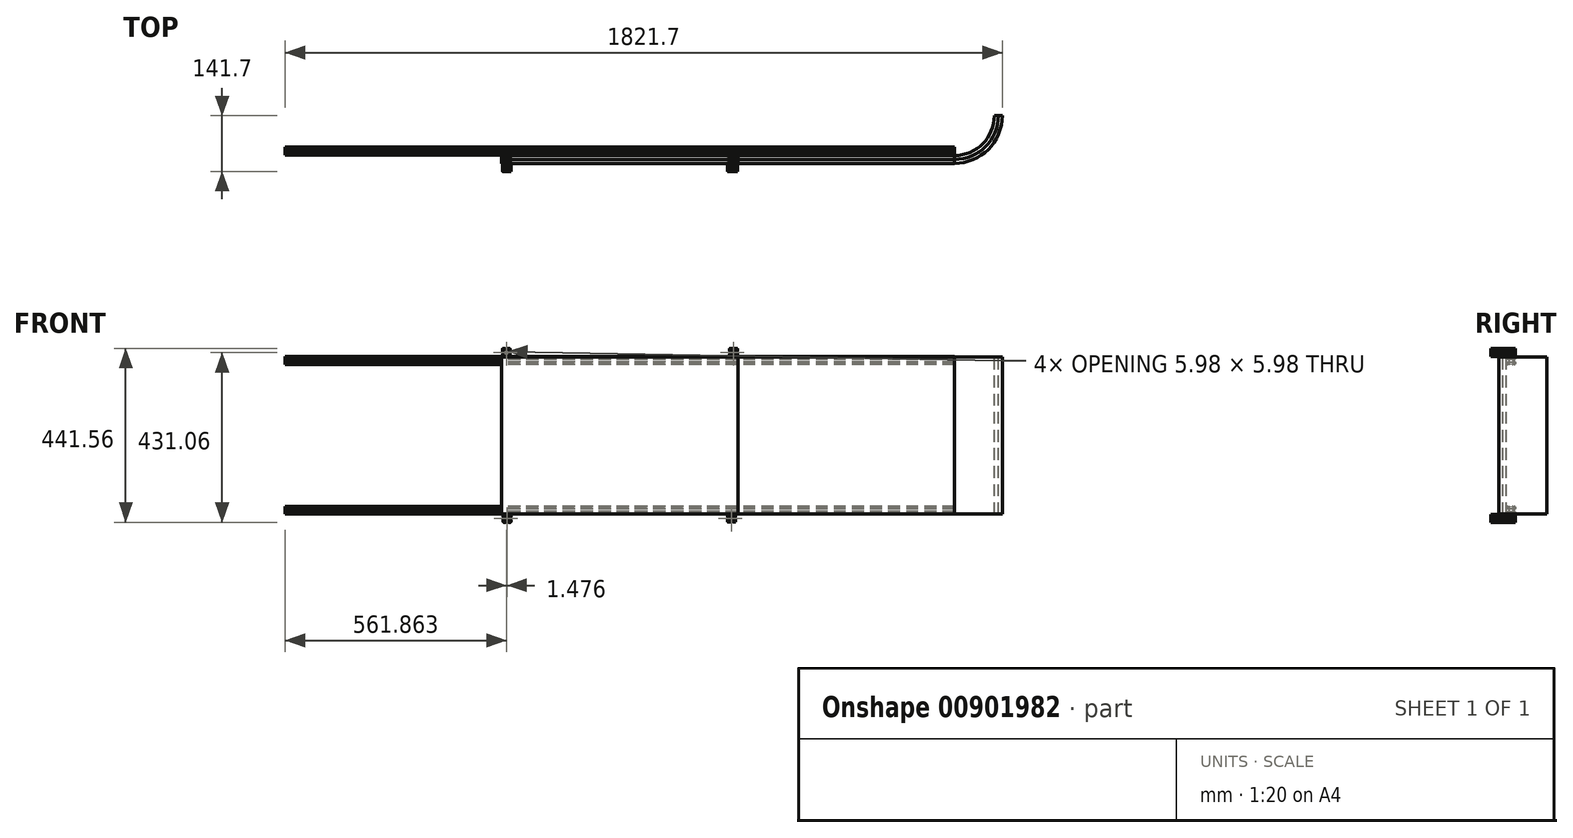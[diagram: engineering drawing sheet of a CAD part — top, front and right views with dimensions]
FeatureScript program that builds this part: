
annotation { "Feature Type Name" : "Feature", "Feature Type Description" : "" }
export const myFeature = defineFeature(function(context is Context, id is Id, definition is map)
    precondition{}
    {
        {
            var Q0;
            Q0=qCreatedBy(makeId("Front.planeOp"),FACE);
            var sketch = newSketch(context, id + "F0", { "sketchPlane" : qUnion([Q0])});
            skLineSegment(sketch, "E0.bottom", {"start": v(300, -200) * mm, "end": v(-300, -200) * mm});
            skLineSegment(sketch, "E0.top", {"start": v(300, 200) * mm, "end": v(-300, 200) * mm});
            skLineSegment(sketch, "E0.left", {"start": v(300, -200) * mm, "end": v(300, 200) * mm});
            skLineSegment(sketch, "E0.right", {"start": v(-300, -200) * mm, "end": v(-300, 200) * mm});
            skPoint(sketch, "E0.middle", {"position": v(0, 0) * mm});
            skSolve(sketch);
        }
        {
            var Q0;
            Q0=makeQuery(id+"F0.imprint","IMPRINT",FACE,{"disambiguationData":[TD([[makeQuery(id+"F0.imprint","IMPRINT",EDGE,{"derivedFrom":sQuery(id+"F0.wireOp",EDGE,"E0.bottom")}),-1.0]])]});
            extrude(context, id + "F1", {"entities" : qUnion([Q0]), "depth" : 10 * mm, "offsetDistance" : 25 * mm});
        }
        {
            var Q0;
            Q0=makeQuery(id+"F1.opExtrude","SWEPT_FACE",FACE,{"disambiguationData":[OSD([sQuery(id+"F0.wireOp",EDGE,"E0.left")])]});
            var sketch = newSketch(context, id + "F2", { "sketchPlane" : qUnion([Q0])});
            skLineSegment(sketch, "E1.bottom", {"start": v(0, -200) * mm, "end": v(-10, -200) * mm});
            skLineSegment(sketch, "E1.top", {"start": v(0, 200) * mm, "end": v(-10, 200) * mm});
            skLineSegment(sketch, "E1.left", {"start": v(0, -200) * mm, "end": v(0, 200) * mm});
            skLineSegment(sketch, "E1.right", {"start": v(-10, -200) * mm, "end": v(-10, 200) * mm});
            skSolve(sketch);
        }
        {
            var Q0;
            Q0=makeQuery(id+"F2.imprint","IMPRINT",FACE,{"disambiguationData":[TD([[makeQuery(id+"F2.imprint","IMPRINT",EDGE,{"derivedFrom":sQuery(id+"F2.wireOp",EDGE,"E1.bottom")}),1.0]])]});
            extrude(context, id + "F3", {"entities" : qUnion([Q0]), "operationType" : NewBodyOperationType.ADD, "depth" : 550 * mm, "offsetDistance" : 25 * mm, "hasSecondDirection" : true, "secondDirectionOppositeDirection" : false, "secondDirectionDepth" : 0.01 * mm});
        }
        {
            var Q0;
            Q0=makeQuery(id+"F3.opExtrude","CAP_FACE",FACE,{"disambiguationData":[OSD([sQuery(id+"F2.wireOp",EDGE,"E1.bottom"),sQuery(id+"F2.wireOp",EDGE,"E1.top"),sQuery(id+"F2.wireOp",EDGE,"E1.left"),sQuery(id+"F2.wireOp",EDGE,"E1.right")])],"isStart":false});
            var sketch = newSketch(context, id + "F4", { "sketchPlane" : qUnion([Q0])});
            skLineSegment(sketch, "E2", {"start": v(0, 0) * mm, "end": v(101.6, 0) * mm});
            skLineSegment(sketch, "E3", {"start": v(101.6, 0) * mm, "end": v(101.6, -197.22) * mm});
            skSolve(sketch);
        }
        {
            var Q0;
            {var subQ1=makeQuery(id+"F3.opExtrude","CAP_EDGE",EDGE,{"disambiguationData":[OSD([sQuery(id+"F2.wireOp",EDGE,"E1.bottom")])],"isStart":false});Q0=makeQuery(id+"F4.imprint","IMPRINT",FACE,{"disambiguationData":[TD([[makeQuery(id+"F4.imprint","IMPRINT",EDGE,{"derivedFrom":subQ1}),1.0]])]});}
            var Q1;
            Q1=sQuery(id+"F4.wireOp",EDGE,"E3");
            revolve(context, id + "F5", {"operationType" : NewBodyOperationType.ADD, "surfaceOperationType" : NewSurfaceOperationType.NEW, "entities" : qUnion([Q0]), "axis" : qUnion([Q1]), "revolveType" : RevolveType.TWO_DIRECTIONS, "angle" : 359.9 * degree, "angleBack" : 270 * degree});
        }
        {
            var Q0;
            Q0=makeQuery(id+"F1.opExtrude","SWEPT_BODY",BODY,{"disambiguationData":[OSD([sQuery(id+"F0.wireOp",EDGE,"E0.bottom"),sQuery(id+"F0.wireOp",EDGE,"E0.top"),sQuery(id+"F0.wireOp",EDGE,"E0.left"),sQuery(id+"F0.wireOp",EDGE,"E0.right")])]});
            transform(context, id + "F6", {"entities" : qUnion([Q0]), "transformType" : TransformType.TRANSLATION_3D, "dx" : 0 * mm, "dy" : -10.1 * mm, "dz" : 0 * mm, "makeCopy" : true});
        }
        {
            var Q0;
            Q0=makeQuery(id+"F3.opExtrude","SWEPT_BODY",BODY,{"disambiguationData":[OSD([sQuery(id+"F2.wireOp",EDGE,"E1.bottom"),sQuery(id+"F2.wireOp",EDGE,"E1.top"),sQuery(id+"F2.wireOp",EDGE,"E1.left"),sQuery(id+"F2.wireOp",EDGE,"E1.right")])]});
            transform(context, id + "F7", {"entities" : qUnion([Q0]), "transformType" : TransformType.TRANSLATION_3D, "dx" : 0 * mm, "dy" : -10.1 * mm, "dz" : 0 * mm, "makeCopy" : true});
        }
        {
            var Q0;
            Q0=makeQuery(id+"F7.opPattern","COPY",FACE,{"derivedFrom":makeQuery(id+"F3.opExtrude","CAP_FACE",FACE,{"disambiguationData":[OSD([sQuery(id+"F2.wireOp",EDGE,"E1.bottom"),sQuery(id+"F2.wireOp",EDGE,"E1.top"),sQuery(id+"F2.wireOp",EDGE,"E1.left"),sQuery(id+"F2.wireOp",EDGE,"E1.right")])],"isStart":false}),"instanceName":"1"});
            var Q1;
            Q1=sQuery(id+"F4.wireOp",EDGE,"E3");
            revolve(context, id + "F8", {"operationType" : NewBodyOperationType.ADD, "surfaceOperationType" : NewSurfaceOperationType.NEW, "entities" : qUnion([Q0]), "axis" : qUnion([Q1]), "revolveType" : RevolveType.TWO_DIRECTIONS, "angle" : 359.9 * degree, "angleBack" : 270 * degree});
        }
        {
            var Q0;
            Q0=makeQuery(id+"F6.opPattern","COPY",FACE,{"derivedFrom":makeQuery(id+"F1.opExtrude","SWEPT_FACE",FACE,{"disambiguationData":[OSD([sQuery(id+"F0.wireOp",EDGE,"E0.right")])]}),"instanceName":"1"});
            var sketch = newSketch(context, id + "F9", { "sketchPlane" : qUnion([Q0])});
            skArc(sketch, "E4", {"start": v(-20.11, 200.08) * mm, "mid": v(-21.17, 199.64) * mm, "end": v(-21.61, 198.58) * mm});
            skLineSegment(sketch, "E5", {"start": v(-21.61, 198.58) * mm, "end": v(-21.61, 193.83) * mm});
            skArc(sketch, "E6", {"start": v(-21.61, 193.83) * mm, "mid": v(-21.55, 193.7) * mm, "end": v(-21.41, 193.63) * mm});
            skLineSegment(sketch, "E7", {"start": v(-21.41, 193.63) * mm, "end": v(-21.31, 193.63) * mm});
            skArc(sketch, "E8", {"start": v(-21.11, 193.43) * mm, "mid": v(-21.17, 193.58) * mm, "end": v(-21.31, 193.63) * mm});
            skLineSegment(sketch, "E9", {"start": v(-21.11, 193.43) * mm, "end": v(-21.11, 193.28) * mm});
            skArc(sketch, "E10", {"start": v(-21.11, 193.28) * mm, "mid": v(-21.05, 193.14) * mm, "end": v(-20.91, 193.08) * mm});
            skLineSegment(sketch, "E11", {"start": v(-20.91, 193.08) * mm, "end": v(-20.61, 193.08) * mm});
            skArc(sketch, "E12", {"start": v(-20.61, 193.08) * mm, "mid": v(-20.26, 193.23) * mm, "end": v(-20.11, 193.58) * mm});
            skLineSegment(sketch, "E13", {"start": v(-20.11, 193.58) * mm, "end": v(-20.11, 195.58) * mm});
            skArc(sketch, "E14", {"start": v(-19.61, 196.08) * mm, "mid": v(-19.96, 195.94) * mm, "end": v(-20.11, 195.58) * mm});
            skLineSegment(sketch, "E15", {"start": v(-19.61, 196.08) * mm, "end": v(-18.88, 196.08) * mm});
            skArc(sketch, "E16", {"start": v(-18.53, 195.94) * mm, "mid": v(-18.69, 196.05) * mm, "end": v(-18.88, 196.08) * mm});
            skLineSegment(sketch, "E17", {"start": v(-18.53, 195.94) * mm, "end": v(-16.26, 193.67) * mm});
            skArc(sketch, "E18", {"start": v(-16.11, 193.32) * mm, "mid": v(-16.15, 193.5) * mm, "end": v(-16.26, 193.67) * mm});
            skLineSegment(sketch, "E19", {"start": v(-16.11, 193.32) * mm, "end": v(-16.11, 191.04) * mm});
            skArc(sketch, "E20", {"start": v(-16.11, 191.04) * mm, "mid": v(-16.1, 190.99) * mm, "end": v(-16.08, 190.94) * mm});
            skLineSegment(sketch, "E21", {"start": v(-16.08, 190.94) * mm, "end": v(-15.65, 190.18) * mm});
            skArc(sketch, "E22", {"start": v(-15.65, 189.98) * mm, "mid": v(-15.62, 190.08) * mm, "end": v(-15.65, 190.18) * mm});
            skLineSegment(sketch, "E23", {"start": v(-15.65, 189.98) * mm, "end": v(-16.08, 189.23) * mm});
            skArc(sketch, "E24", {"start": v(-16.08, 189.23) * mm, "mid": v(-16.1, 189.18) * mm, "end": v(-16.11, 189.13) * mm});
            skLineSegment(sketch, "E25", {"start": v(-16.11, 189.13) * mm, "end": v(-16.11, 186.85) * mm});
            skArc(sketch, "E26", {"start": v(-16.26, 186.5) * mm, "mid": v(-16.15, 186.66) * mm, "end": v(-16.11, 186.85) * mm});
            skLineSegment(sketch, "E27", {"start": v(-16.26, 186.5) * mm, "end": v(-18.53, 184.23) * mm});
            skArc(sketch, "E28", {"start": v(-18.88, 184.08) * mm, "mid": v(-18.69, 184.12) * mm, "end": v(-18.53, 184.23) * mm});
            skLineSegment(sketch, "E29", {"start": v(-18.88, 184.08) * mm, "end": v(-19.61, 184.08) * mm});
            skArc(sketch, "E30", {"start": v(-20.11, 184.58) * mm, "mid": v(-19.96, 184.23) * mm, "end": v(-19.61, 184.08) * mm});
            skLineSegment(sketch, "E31", {"start": v(-20.11, 184.58) * mm, "end": v(-20.11, 186.58) * mm});
            skArc(sketch, "E32", {"start": v(-20.11, 186.58) * mm, "mid": v(-20.26, 186.94) * mm, "end": v(-20.61, 187.08) * mm});
            skLineSegment(sketch, "E33", {"start": v(-20.61, 187.08) * mm, "end": v(-20.91, 187.08) * mm});
            skArc(sketch, "E34", {"start": v(-20.91, 187.08) * mm, "mid": v(-21.05, 187.03) * mm, "end": v(-21.11, 186.88) * mm});
            skLineSegment(sketch, "E35", {"start": v(-21.11, 186.88) * mm, "end": v(-21.11, 186.73) * mm});
            skArc(sketch, "E36", {"start": v(-21.31, 186.53) * mm, "mid": v(-21.17, 186.6) * mm, "end": v(-21.11, 186.73) * mm});
            skLineSegment(sketch, "E37", {"start": v(-21.31, 186.53) * mm, "end": v(-21.41, 186.53) * mm});
            skArc(sketch, "E38", {"start": v(-21.41, 186.53) * mm, "mid": v(-21.55, 186.48) * mm, "end": v(-21.61, 186.33) * mm});
            skLineSegment(sketch, "E39", {"start": v(-21.61, 186.33) * mm, "end": v(-21.61, 181.58) * mm});
            skArc(sketch, "E40", {"start": v(-21.61, 181.58) * mm, "mid": v(-21.17, 180.52) * mm, "end": v(-20.11, 180.08) * mm});
            skLineSegment(sketch, "E41", {"start": v(-20.11, 180.08) * mm, "end": v(-15.36, 180.08) * mm});
            skArc(sketch, "E42", {"start": v(-15.36, 180.08) * mm, "mid": v(-15.22, 180.14) * mm, "end": v(-15.16, 180.28) * mm});
            skLineSegment(sketch, "E43", {"start": v(-15.16, 180.28) * mm, "end": v(-15.16, 180.38) * mm});
            skArc(sketch, "E44", {"start": v(-14.96, 180.58) * mm, "mid": v(-15.1, 180.53) * mm, "end": v(-15.16, 180.38) * mm});
            skLineSegment(sketch, "E45", {"start": v(-14.96, 180.58) * mm, "end": v(-14.81, 180.58) * mm});
            skArc(sketch, "E46", {"start": v(-14.81, 180.58) * mm, "mid": v(-14.67, 180.64) * mm, "end": v(-14.61, 180.78) * mm});
            skLineSegment(sketch, "E47", {"start": v(-14.61, 180.78) * mm, "end": v(-14.61, 181.08) * mm});
            skArc(sketch, "E48", {"start": v(-14.61, 181.08) * mm, "mid": v(-14.76, 181.44) * mm, "end": v(-15.11, 181.58) * mm});
            skLineSegment(sketch, "E49", {"start": v(-15.11, 181.58) * mm, "end": v(-17.11, 181.58) * mm});
            skArc(sketch, "E50", {"start": v(-17.61, 182.08) * mm, "mid": v(-17.46, 181.73) * mm, "end": v(-17.11, 181.58) * mm});
            skLineSegment(sketch, "E51", {"start": v(-17.61, 182.08) * mm, "end": v(-17.61, 182.82) * mm});
            skArc(sketch, "E52", {"start": v(-17.46, 183.17) * mm, "mid": v(-17.57, 183) * mm, "end": v(-17.61, 182.82) * mm});
            skLineSegment(sketch, "E53", {"start": v(-17.46, 183.17) * mm, "end": v(-15.2, 185.44) * mm});
            skArc(sketch, "E54", {"start": v(-14.84, 185.58) * mm, "mid": v(-15.03, 185.55) * mm, "end": v(-15.2, 185.44) * mm});
            skLineSegment(sketch, "E55", {"start": v(-14.84, 185.58) * mm, "end": v(-12.56, 185.58) * mm});
            skArc(sketch, "E56", {"start": v(-12.56, 185.58) * mm, "mid": v(-12.51, 185.6) * mm, "end": v(-12.46, 185.61) * mm});
            skLineSegment(sketch, "E57", {"start": v(-12.46, 185.61) * mm, "end": v(-11.71, 186.05) * mm});
            skArc(sketch, "E58", {"start": v(-11.51, 186.05) * mm, "mid": v(-11.61, 186.07) * mm, "end": v(-11.71, 186.05) * mm});
            skLineSegment(sketch, "E59", {"start": v(-11.51, 186.05) * mm, "end": v(-10.76, 185.61) * mm});
            skArc(sketch, "E60", {"start": v(-10.76, 185.61) * mm, "mid": v(-10.7, 185.6) * mm, "end": v(-10.66, 185.58) * mm});
            skLineSegment(sketch, "E61", {"start": v(-10.66, 185.58) * mm, "end": v(-8.38, 185.58) * mm});
            skArc(sketch, "E62", {"start": v(-8.03, 185.44) * mm, "mid": v(-8.19, 185.55) * mm, "end": v(-8.38, 185.58) * mm});
            skLineSegment(sketch, "E63", {"start": v(-8.03, 185.44) * mm, "end": v(-5.76, 183.17) * mm});
            skArc(sketch, "E64", {"start": v(-5.61, 182.82) * mm, "mid": v(-5.65, 183) * mm, "end": v(-5.76, 183.17) * mm});
            skLineSegment(sketch, "E65", {"start": v(-5.61, 182.82) * mm, "end": v(-5.61, 182.08) * mm});
            skArc(sketch, "E66", {"start": v(-6.11, 181.58) * mm, "mid": v(-5.76, 181.73) * mm, "end": v(-5.61, 182.08) * mm});
            skLineSegment(sketch, "E67", {"start": v(-6.11, 181.58) * mm, "end": v(-8.11, 181.58) * mm});
            skArc(sketch, "E68", {"start": v(-8.11, 181.58) * mm, "mid": v(-8.46, 181.44) * mm, "end": v(-8.61, 181.08) * mm});
            skLineSegment(sketch, "E69", {"start": v(-8.61, 181.08) * mm, "end": v(-8.61, 180.78) * mm});
            skArc(sketch, "E70", {"start": v(-8.61, 180.78) * mm, "mid": v(-8.55, 180.64) * mm, "end": v(-8.41, 180.58) * mm});
            skLineSegment(sketch, "E71", {"start": v(-8.41, 180.58) * mm, "end": v(-8.26, 180.58) * mm});
            skArc(sketch, "E72", {"start": v(-8.06, 180.38) * mm, "mid": v(-8.12, 180.53) * mm, "end": v(-8.26, 180.58) * mm});
            skLineSegment(sketch, "E73", {"start": v(-8.06, 180.38) * mm, "end": v(-8.06, 180.28) * mm});
            skArc(sketch, "E74", {"start": v(-8.06, 180.28) * mm, "mid": v(-8, 180.14) * mm, "end": v(-7.86, 180.08) * mm});
            skLineSegment(sketch, "E75", {"start": v(-7.86, 180.08) * mm, "end": v(-3.11, 180.08) * mm});
            skArc(sketch, "E76", {"start": v(-3.11, 180.08) * mm, "mid": v(-2.05, 180.52) * mm, "end": v(-1.61, 181.58) * mm});
            skLineSegment(sketch, "E77", {"start": v(-1.61, 181.58) * mm, "end": v(-1.61, 186.33) * mm});
            skArc(sketch, "E78", {"start": v(-1.61, 186.33) * mm, "mid": v(-1.67, 186.48) * mm, "end": v(-1.81, 186.53) * mm});
            skLineSegment(sketch, "E79", {"start": v(-1.81, 186.53) * mm, "end": v(-1.91, 186.53) * mm});
            skArc(sketch, "E80", {"start": v(-2.11, 186.73) * mm, "mid": v(-2.05, 186.6) * mm, "end": v(-1.91, 186.53) * mm});
            skLineSegment(sketch, "E81", {"start": v(-2.11, 186.73) * mm, "end": v(-2.11, 186.88) * mm});
            skArc(sketch, "E82", {"start": v(-2.11, 186.88) * mm, "mid": v(-2.17, 187.03) * mm, "end": v(-2.31, 187.08) * mm});
            skLineSegment(sketch, "E83", {"start": v(-2.31, 187.08) * mm, "end": v(-2.61, 187.08) * mm});
            skArc(sketch, "E84", {"start": v(-2.61, 187.08) * mm, "mid": v(-2.96, 186.94) * mm, "end": v(-3.11, 186.58) * mm});
            skLineSegment(sketch, "E85", {"start": v(-3.11, 186.58) * mm, "end": v(-3.11, 184.58) * mm});
            skArc(sketch, "E86", {"start": v(-3.61, 184.08) * mm, "mid": v(-3.26, 184.23) * mm, "end": v(-3.11, 184.58) * mm});
            skLineSegment(sketch, "E87", {"start": v(-3.61, 184.08) * mm, "end": v(-4.34, 184.08) * mm});
            skArc(sketch, "E88", {"start": v(-4.7, 184.23) * mm, "mid": v(-4.53, 184.12) * mm, "end": v(-4.34, 184.08) * mm});
            skLineSegment(sketch, "E89", {"start": v(-4.7, 184.23) * mm, "end": v(-6.96, 186.5) * mm});
            skArc(sketch, "E90", {"start": v(-7.11, 186.85) * mm, "mid": v(-7.07, 186.66) * mm, "end": v(-6.96, 186.5) * mm});
            skLineSegment(sketch, "E91", {"start": v(-7.11, 186.85) * mm, "end": v(-7.11, 189.13) * mm});
            skArc(sketch, "E92", {"start": v(-7.11, 189.13) * mm, "mid": v(-7.12, 189.18) * mm, "end": v(-7.14, 189.23) * mm});
            skLineSegment(sketch, "E93", {"start": v(-7.14, 189.23) * mm, "end": v(-7.57, 189.98) * mm});
            skArc(sketch, "E94", {"start": v(-7.57, 190.18) * mm, "mid": v(-7.6, 190.08) * mm, "end": v(-7.57, 189.98) * mm});
            skLineSegment(sketch, "E95", {"start": v(-7.57, 190.18) * mm, "end": v(-7.14, 190.94) * mm});
            skArc(sketch, "E96", {"start": v(-7.14, 190.94) * mm, "mid": v(-7.12, 190.99) * mm, "end": v(-7.11, 191.04) * mm});
            skLineSegment(sketch, "E97", {"start": v(-7.11, 191.04) * mm, "end": v(-7.11, 193.32) * mm});
            skArc(sketch, "E98", {"start": v(-6.96, 193.67) * mm, "mid": v(-7.07, 193.5) * mm, "end": v(-7.11, 193.32) * mm});
            skLineSegment(sketch, "E99", {"start": v(-6.96, 193.67) * mm, "end": v(-4.7, 195.94) * mm});
            skArc(sketch, "E100", {"start": v(-4.34, 196.08) * mm, "mid": v(-4.53, 196.05) * mm, "end": v(-4.7, 195.94) * mm});
            skLineSegment(sketch, "E101", {"start": v(-4.34, 196.08) * mm, "end": v(-3.61, 196.08) * mm});
            skArc(sketch, "E102", {"start": v(-3.11, 195.58) * mm, "mid": v(-3.26, 195.94) * mm, "end": v(-3.61, 196.08) * mm});
            skLineSegment(sketch, "E103", {"start": v(-3.11, 195.58) * mm, "end": v(-3.11, 193.58) * mm});
            skArc(sketch, "E104", {"start": v(-3.11, 193.58) * mm, "mid": v(-2.96, 193.23) * mm, "end": v(-2.61, 193.08) * mm});
            skLineSegment(sketch, "E105", {"start": v(-2.61, 193.08) * mm, "end": v(-2.31, 193.08) * mm});
            skArc(sketch, "E106", {"start": v(-2.31, 193.08) * mm, "mid": v(-2.17, 193.14) * mm, "end": v(-2.11, 193.28) * mm});
            skLineSegment(sketch, "E107", {"start": v(-2.11, 193.28) * mm, "end": v(-2.11, 193.43) * mm});
            skArc(sketch, "E108", {"start": v(-1.91, 193.63) * mm, "mid": v(-2.05, 193.58) * mm, "end": v(-2.11, 193.43) * mm});
            skLineSegment(sketch, "E109", {"start": v(-1.91, 193.63) * mm, "end": v(-1.81, 193.63) * mm});
            skArc(sketch, "E110", {"start": v(-1.81, 193.63) * mm, "mid": v(-1.67, 193.7) * mm, "end": v(-1.61, 193.83) * mm});
            skLineSegment(sketch, "E111", {"start": v(-1.61, 193.83) * mm, "end": v(-1.61, 198.58) * mm});
            skArc(sketch, "E112", {"start": v(-1.61, 198.58) * mm, "mid": v(-2.05, 199.64) * mm, "end": v(-3.11, 200.08) * mm});
            skLineSegment(sketch, "E113", {"start": v(-3.11, 200.08) * mm, "end": v(-7.86, 200.08) * mm});
            skArc(sketch, "E114", {"start": v(-7.86, 200.08) * mm, "mid": v(-8, 200.03) * mm, "end": v(-8.06, 199.88) * mm});
            skLineSegment(sketch, "E115", {"start": v(-8.06, 199.88) * mm, "end": v(-8.06, 199.78) * mm});
            skArc(sketch, "E116", {"start": v(-8.26, 199.58) * mm, "mid": v(-8.12, 199.64) * mm, "end": v(-8.06, 199.78) * mm});
            skLineSegment(sketch, "E117", {"start": v(-8.26, 199.58) * mm, "end": v(-8.41, 199.58) * mm});
            skArc(sketch, "E118", {"start": v(-8.41, 199.58) * mm, "mid": v(-8.55, 199.53) * mm, "end": v(-8.61, 199.38) * mm});
            skLineSegment(sketch, "E119", {"start": v(-8.61, 199.38) * mm, "end": v(-8.61, 199.08) * mm});
            skArc(sketch, "E120", {"start": v(-8.61, 199.08) * mm, "mid": v(-8.46, 198.73) * mm, "end": v(-8.11, 198.58) * mm});
            skLineSegment(sketch, "E121", {"start": v(-8.11, 198.58) * mm, "end": v(-6.11, 198.58) * mm});
            skArc(sketch, "E122", {"start": v(-5.61, 198.08) * mm, "mid": v(-5.76, 198.44) * mm, "end": v(-6.11, 198.58) * mm});
            skLineSegment(sketch, "E123", {"start": v(-5.61, 198.08) * mm, "end": v(-5.61, 197.35) * mm});
            skArc(sketch, "E124", {"start": v(-5.76, 197) * mm, "mid": v(-5.65, 197.16) * mm, "end": v(-5.61, 197.35) * mm});
            skLineSegment(sketch, "E125", {"start": v(-5.76, 197) * mm, "end": v(-8.03, 194.73) * mm});
            skArc(sketch, "E126", {"start": v(-8.38, 194.58) * mm, "mid": v(-8.19, 194.62) * mm, "end": v(-8.03, 194.73) * mm});
            skLineSegment(sketch, "E127", {"start": v(-8.38, 194.58) * mm, "end": v(-10.66, 194.58) * mm});
            skArc(sketch, "E128", {"start": v(-10.66, 194.58) * mm, "mid": v(-10.7, 194.58) * mm, "end": v(-10.76, 194.56) * mm});
            skLineSegment(sketch, "E129", {"start": v(-10.76, 194.56) * mm, "end": v(-11.51, 194.12) * mm});
            skArc(sketch, "E130", {"start": v(-11.71, 194.12) * mm, "mid": v(-11.61, 194.1) * mm, "end": v(-11.51, 194.12) * mm});
            skLineSegment(sketch, "E131", {"start": v(-11.71, 194.12) * mm, "end": v(-12.46, 194.56) * mm});
            skArc(sketch, "E132", {"start": v(-12.46, 194.56) * mm, "mid": v(-12.51, 194.58) * mm, "end": v(-12.56, 194.58) * mm});
            skLineSegment(sketch, "E133", {"start": v(-12.56, 194.58) * mm, "end": v(-14.84, 194.58) * mm});
            skArc(sketch, "E134", {"start": v(-15.2, 194.73) * mm, "mid": v(-15.03, 194.62) * mm, "end": v(-14.84, 194.58) * mm});
            skLineSegment(sketch, "E135", {"start": v(-15.2, 194.73) * mm, "end": v(-17.46, 197) * mm});
            skArc(sketch, "E136", {"start": v(-17.61, 197.35) * mm, "mid": v(-17.57, 197.16) * mm, "end": v(-17.46, 197) * mm});
            skLineSegment(sketch, "E137", {"start": v(-17.61, 197.35) * mm, "end": v(-17.61, 198.08) * mm});
            skArc(sketch, "E138", {"start": v(-17.11, 198.58) * mm, "mid": v(-17.46, 198.44) * mm, "end": v(-17.61, 198.08) * mm});
            skLineSegment(sketch, "E139", {"start": v(-17.11, 198.58) * mm, "end": v(-15.11, 198.58) * mm});
            skArc(sketch, "E140", {"start": v(-15.11, 198.58) * mm, "mid": v(-14.76, 198.73) * mm, "end": v(-14.61, 199.08) * mm});
            skLineSegment(sketch, "E141", {"start": v(-14.61, 199.08) * mm, "end": v(-14.61, 199.38) * mm});
            skArc(sketch, "E142", {"start": v(-14.61, 199.38) * mm, "mid": v(-14.67, 199.53) * mm, "end": v(-14.81, 199.58) * mm});
            skLineSegment(sketch, "E143", {"start": v(-14.81, 199.58) * mm, "end": v(-14.96, 199.58) * mm});
            skArc(sketch, "E144", {"start": v(-15.16, 199.78) * mm, "mid": v(-15.1, 199.64) * mm, "end": v(-14.96, 199.58) * mm});
            skLineSegment(sketch, "E145", {"start": v(-15.16, 199.78) * mm, "end": v(-15.16, 199.88) * mm});
            skArc(sketch, "E146", {"start": v(-15.16, 199.88) * mm, "mid": v(-15.22, 200.03) * mm, "end": v(-15.36, 200.08) * mm});
            skLineSegment(sketch, "E147", {"start": v(-15.36, 200.08) * mm, "end": v(-20.11, 200.08) * mm});
            skArc(sketch, "E148", {"start": v(-13.52, 193.07) * mm, "mid": v(-14.12, 192.6) * mm, "end": v(-14.6, 192) * mm});
            skLineSegment(sketch, "E149", {"start": v(-12.87, 192.53) * mm, "end": v(-13.52, 193.07) * mm});
            skArc(sketch, "E150", {"start": v(-10.35, 192.53) * mm, "mid": v(-11.61, 192.83) * mm, "end": v(-12.87, 192.53) * mm});
            skLineSegment(sketch, "E151", {"start": v(-9.7, 193.07) * mm, "end": v(-10.35, 192.53) * mm});
            skArc(sketch, "E152", {"start": v(-8.62, 192) * mm, "mid": v(-9.1, 192.6) * mm, "end": v(-9.7, 193.07) * mm});
            skLineSegment(sketch, "E153", {"start": v(-9.17, 191.34) * mm, "end": v(-8.62, 192) * mm});
            skArc(sketch, "E154", {"start": v(-9.17, 188.83) * mm, "mid": v(-8.86, 190.08) * mm, "end": v(-9.17, 191.34) * mm});
            skLineSegment(sketch, "E155", {"start": v(-8.62, 188.17) * mm, "end": v(-9.17, 188.83) * mm});
            skArc(sketch, "E156", {"start": v(-9.7, 187.1) * mm, "mid": v(-9.1, 187.58) * mm, "end": v(-8.62, 188.17) * mm});
            skLineSegment(sketch, "E157", {"start": v(-10.35, 187.64) * mm, "end": v(-9.7, 187.1) * mm});
            skArc(sketch, "E158", {"start": v(-12.87, 187.64) * mm, "mid": v(-11.61, 187.33) * mm, "end": v(-10.35, 187.64) * mm});
            skLineSegment(sketch, "E159", {"start": v(-13.52, 187.1) * mm, "end": v(-12.87, 187.64) * mm});
            skArc(sketch, "E160", {"start": v(-14.6, 188.17) * mm, "mid": v(-14.12, 187.58) * mm, "end": v(-13.52, 187.1) * mm});
            skLineSegment(sketch, "E161", {"start": v(-14.06, 188.83) * mm, "end": v(-14.6, 188.17) * mm});
            skArc(sketch, "E162", {"start": v(-14.06, 191.34) * mm, "mid": v(-14.36, 190.08) * mm, "end": v(-14.06, 188.83) * mm});
            skLineSegment(sketch, "E163", {"start": v(-14.6, 192) * mm, "end": v(-14.06, 191.34) * mm});
            skArc(sketch, "E164", {"start": v(-20.11, -180) * mm, "mid": v(-21.17, -180.44) * mm, "end": v(-21.61, -181.5) * mm});
            skLineSegment(sketch, "E165", {"start": v(-21.61, -181.5) * mm, "end": v(-21.61, -186.25) * mm});
            skArc(sketch, "E166", {"start": v(-21.61, -186.25) * mm, "mid": v(-21.55, -186.4) * mm, "end": v(-21.41, -186.45) * mm});
            skLineSegment(sketch, "E167", {"start": v(-21.41, -186.45) * mm, "end": v(-21.31, -186.45) * mm});
            skArc(sketch, "E168", {"start": v(-21.11, -186.65) * mm, "mid": v(-21.17, -186.5) * mm, "end": v(-21.31, -186.45) * mm});
            skLineSegment(sketch, "E169", {"start": v(-21.11, -186.65) * mm, "end": v(-21.11, -186.8) * mm});
            skArc(sketch, "E170", {"start": v(-21.11, -186.8) * mm, "mid": v(-21.05, -186.94) * mm, "end": v(-20.91, -187) * mm});
            skLineSegment(sketch, "E171", {"start": v(-20.91, -187) * mm, "end": v(-20.61, -187) * mm});
            skArc(sketch, "E172", {"start": v(-20.61, -187) * mm, "mid": v(-20.26, -186.85) * mm, "end": v(-20.11, -186.5) * mm});
            skLineSegment(sketch, "E173", {"start": v(-20.11, -186.5) * mm, "end": v(-20.11, -184.5) * mm});
            skArc(sketch, "E174", {"start": v(-19.61, -184) * mm, "mid": v(-19.96, -184.15) * mm, "end": v(-20.11, -184.5) * mm});
            skLineSegment(sketch, "E175", {"start": v(-19.61, -184) * mm, "end": v(-18.88, -184) * mm});
            skArc(sketch, "E176", {"start": v(-18.53, -184.15) * mm, "mid": v(-18.69, -184.04) * mm, "end": v(-18.88, -184) * mm});
            skLineSegment(sketch, "E177", {"start": v(-18.53, -184.15) * mm, "end": v(-16.26, -186.41) * mm});
            skArc(sketch, "E178", {"start": v(-16.11, -186.77) * mm, "mid": v(-16.15, -186.58) * mm, "end": v(-16.26, -186.41) * mm});
            skLineSegment(sketch, "E179", {"start": v(-16.11, -186.77) * mm, "end": v(-16.11, -189.05) * mm});
            skArc(sketch, "E180", {"start": v(-16.11, -189.05) * mm, "mid": v(-16.1, -189.1) * mm, "end": v(-16.08, -189.15) * mm});
            skLineSegment(sketch, "E181", {"start": v(-16.08, -189.15) * mm, "end": v(-15.65, -189.9) * mm});
            skArc(sketch, "E182", {"start": v(-15.65, -190.1) * mm, "mid": v(-15.62, -190) * mm, "end": v(-15.65, -189.9) * mm});
            skLineSegment(sketch, "E183", {"start": v(-15.65, -190.1) * mm, "end": v(-16.08, -190.85) * mm});
            skArc(sketch, "E184", {"start": v(-16.08, -190.85) * mm, "mid": v(-16.1, -190.9) * mm, "end": v(-16.11, -190.95) * mm});
            skLineSegment(sketch, "E185", {"start": v(-16.11, -190.95) * mm, "end": v(-16.11, -193.23) * mm});
            skArc(sketch, "E186", {"start": v(-16.26, -193.59) * mm, "mid": v(-16.15, -193.42) * mm, "end": v(-16.11, -193.23) * mm});
            skLineSegment(sketch, "E187", {"start": v(-16.26, -193.59) * mm, "end": v(-18.53, -195.85) * mm});
            skArc(sketch, "E188", {"start": v(-18.88, -196) * mm, "mid": v(-18.69, -195.96) * mm, "end": v(-18.53, -195.85) * mm});
            skLineSegment(sketch, "E189", {"start": v(-18.88, -196) * mm, "end": v(-19.61, -196) * mm});
            skArc(sketch, "E190", {"start": v(-20.11, -195.5) * mm, "mid": v(-19.96, -195.85) * mm, "end": v(-19.61, -196) * mm});
            skLineSegment(sketch, "E191", {"start": v(-20.11, -195.5) * mm, "end": v(-20.11, -193.5) * mm});
            skArc(sketch, "E192", {"start": v(-20.11, -193.5) * mm, "mid": v(-20.26, -193.15) * mm, "end": v(-20.61, -193) * mm});
            skLineSegment(sketch, "E193", {"start": v(-20.61, -193) * mm, "end": v(-20.91, -193) * mm});
            skArc(sketch, "E194", {"start": v(-20.91, -193) * mm, "mid": v(-21.05, -193.06) * mm, "end": v(-21.11, -193.2) * mm});
            skLineSegment(sketch, "E195", {"start": v(-21.11, -193.2) * mm, "end": v(-21.11, -193.35) * mm});
            skArc(sketch, "E196", {"start": v(-21.31, -193.55) * mm, "mid": v(-21.17, -193.5) * mm, "end": v(-21.11, -193.35) * mm});
            skLineSegment(sketch, "E197", {"start": v(-21.31, -193.55) * mm, "end": v(-21.41, -193.55) * mm});
            skArc(sketch, "E198", {"start": v(-21.41, -193.55) * mm, "mid": v(-21.55, -193.6) * mm, "end": v(-21.61, -193.75) * mm});
            skLineSegment(sketch, "E199", {"start": v(-21.61, -193.75) * mm, "end": v(-21.61, -198.5) * mm});
            skArc(sketch, "E200", {"start": v(-21.61, -198.5) * mm, "mid": v(-21.17, -199.56) * mm, "end": v(-20.11, -200) * mm});
            skLineSegment(sketch, "E201", {"start": v(-20.11, -200) * mm, "end": v(-15.36, -200) * mm});
            skArc(sketch, "E202", {"start": v(-15.36, -200) * mm, "mid": v(-15.22, -199.94) * mm, "end": v(-15.16, -199.8) * mm});
            skLineSegment(sketch, "E203", {"start": v(-15.16, -199.8) * mm, "end": v(-15.16, -199.7) * mm});
            skArc(sketch, "E204", {"start": v(-14.96, -199.5) * mm, "mid": v(-15.1, -199.56) * mm, "end": v(-15.16, -199.7) * mm});
            skLineSegment(sketch, "E205", {"start": v(-14.96, -199.5) * mm, "end": v(-14.81, -199.5) * mm});
            skArc(sketch, "E206", {"start": v(-14.81, -199.5) * mm, "mid": v(-14.67, -199.44) * mm, "end": v(-14.61, -199.3) * mm});
            skLineSegment(sketch, "E207", {"start": v(-14.61, -199.3) * mm, "end": v(-14.61, -199) * mm});
            skArc(sketch, "E208", {"start": v(-14.61, -199) * mm, "mid": v(-14.76, -198.65) * mm, "end": v(-15.11, -198.5) * mm});
            skLineSegment(sketch, "E209", {"start": v(-15.11, -198.5) * mm, "end": v(-17.11, -198.5) * mm});
            skArc(sketch, "E210", {"start": v(-17.61, -198) * mm, "mid": v(-17.46, -198.35) * mm, "end": v(-17.11, -198.5) * mm});
            skLineSegment(sketch, "E211", {"start": v(-17.61, -198) * mm, "end": v(-17.61, -197.27) * mm});
            skArc(sketch, "E212", {"start": v(-17.46, -196.91) * mm, "mid": v(-17.57, -197.08) * mm, "end": v(-17.61, -197.27) * mm});
            skLineSegment(sketch, "E213", {"start": v(-17.46, -196.91) * mm, "end": v(-15.2, -194.65) * mm});
            skArc(sketch, "E214", {"start": v(-14.84, -194.5) * mm, "mid": v(-15.03, -194.54) * mm, "end": v(-15.2, -194.65) * mm});
            skLineSegment(sketch, "E215", {"start": v(-14.84, -194.5) * mm, "end": v(-12.56, -194.5) * mm});
            skArc(sketch, "E216", {"start": v(-12.56, -194.5) * mm, "mid": v(-12.51, -194.5) * mm, "end": v(-12.46, -194.47) * mm});
            skLineSegment(sketch, "E217", {"start": v(-12.46, -194.47) * mm, "end": v(-11.71, -194.04) * mm});
            skArc(sketch, "E218", {"start": v(-11.51, -194.04) * mm, "mid": v(-11.61, -194.01) * mm, "end": v(-11.71, -194.04) * mm});
            skLineSegment(sketch, "E219", {"start": v(-11.51, -194.04) * mm, "end": v(-10.76, -194.47) * mm});
            skArc(sketch, "E220", {"start": v(-10.76, -194.47) * mm, "mid": v(-10.7, -194.5) * mm, "end": v(-10.66, -194.5) * mm});
            skLineSegment(sketch, "E221", {"start": v(-10.66, -194.5) * mm, "end": v(-8.38, -194.5) * mm});
            skArc(sketch, "E222", {"start": v(-8.03, -194.65) * mm, "mid": v(-8.19, -194.54) * mm, "end": v(-8.38, -194.5) * mm});
            skLineSegment(sketch, "E223", {"start": v(-8.03, -194.65) * mm, "end": v(-5.76, -196.91) * mm});
            skArc(sketch, "E224", {"start": v(-5.61, -197.27) * mm, "mid": v(-5.65, -197.08) * mm, "end": v(-5.76, -196.91) * mm});
            skLineSegment(sketch, "E225", {"start": v(-5.61, -197.27) * mm, "end": v(-5.61, -198) * mm});
            skArc(sketch, "E226", {"start": v(-6.11, -198.5) * mm, "mid": v(-5.76, -198.35) * mm, "end": v(-5.61, -198) * mm});
            skLineSegment(sketch, "E227", {"start": v(-6.11, -198.5) * mm, "end": v(-8.11, -198.5) * mm});
            skArc(sketch, "E228", {"start": v(-8.11, -198.5) * mm, "mid": v(-8.46, -198.65) * mm, "end": v(-8.61, -199) * mm});
            skLineSegment(sketch, "E229", {"start": v(-8.61, -199) * mm, "end": v(-8.61, -199.3) * mm});
            skArc(sketch, "E230", {"start": v(-8.61, -199.3) * mm, "mid": v(-8.55, -199.44) * mm, "end": v(-8.41, -199.5) * mm});
            skLineSegment(sketch, "E231", {"start": v(-8.41, -199.5) * mm, "end": v(-8.26, -199.5) * mm});
            skArc(sketch, "E232", {"start": v(-8.06, -199.7) * mm, "mid": v(-8.12, -199.56) * mm, "end": v(-8.26, -199.5) * mm});
            skLineSegment(sketch, "E233", {"start": v(-8.06, -199.7) * mm, "end": v(-8.06, -199.8) * mm});
            skArc(sketch, "E234", {"start": v(-8.06, -199.8) * mm, "mid": v(-8, -199.94) * mm, "end": v(-7.86, -200) * mm});
            skLineSegment(sketch, "E235", {"start": v(-7.86, -200) * mm, "end": v(-3.11, -200) * mm});
            skArc(sketch, "E236", {"start": v(-3.11, -200) * mm, "mid": v(-2.05, -199.56) * mm, "end": v(-1.61, -198.5) * mm});
            skLineSegment(sketch, "E237", {"start": v(-1.61, -198.5) * mm, "end": v(-1.61, -193.75) * mm});
            skArc(sketch, "E238", {"start": v(-1.61, -193.75) * mm, "mid": v(-1.67, -193.6) * mm, "end": v(-1.81, -193.55) * mm});
            skLineSegment(sketch, "E239", {"start": v(-1.81, -193.55) * mm, "end": v(-1.91, -193.55) * mm});
            skArc(sketch, "E240", {"start": v(-2.11, -193.35) * mm, "mid": v(-2.05, -193.5) * mm, "end": v(-1.91, -193.55) * mm});
            skLineSegment(sketch, "E241", {"start": v(-2.11, -193.35) * mm, "end": v(-2.11, -193.2) * mm});
            skArc(sketch, "E242", {"start": v(-2.11, -193.2) * mm, "mid": v(-2.17, -193.06) * mm, "end": v(-2.31, -193) * mm});
            skLineSegment(sketch, "E243", {"start": v(-2.31, -193) * mm, "end": v(-2.61, -193) * mm});
            skArc(sketch, "E244", {"start": v(-2.61, -193) * mm, "mid": v(-2.96, -193.15) * mm, "end": v(-3.11, -193.5) * mm});
            skLineSegment(sketch, "E245", {"start": v(-3.11, -193.5) * mm, "end": v(-3.11, -195.5) * mm});
            skArc(sketch, "E246", {"start": v(-3.61, -196) * mm, "mid": v(-3.26, -195.85) * mm, "end": v(-3.11, -195.5) * mm});
            skLineSegment(sketch, "E247", {"start": v(-3.61, -196) * mm, "end": v(-4.34, -196) * mm});
            skArc(sketch, "E248", {"start": v(-4.7, -195.85) * mm, "mid": v(-4.53, -195.96) * mm, "end": v(-4.34, -196) * mm});
            skLineSegment(sketch, "E249", {"start": v(-4.7, -195.85) * mm, "end": v(-6.96, -193.59) * mm});
            skArc(sketch, "E250", {"start": v(-7.11, -193.23) * mm, "mid": v(-7.07, -193.42) * mm, "end": v(-6.96, -193.59) * mm});
            skLineSegment(sketch, "E251", {"start": v(-7.11, -193.23) * mm, "end": v(-7.11, -190.95) * mm});
            skArc(sketch, "E252", {"start": v(-7.11, -190.95) * mm, "mid": v(-7.12, -190.9) * mm, "end": v(-7.14, -190.85) * mm});
            skLineSegment(sketch, "E253", {"start": v(-7.14, -190.85) * mm, "end": v(-7.57, -190.1) * mm});
            skArc(sketch, "E254", {"start": v(-7.57, -189.9) * mm, "mid": v(-7.6, -190) * mm, "end": v(-7.57, -190.1) * mm});
            skLineSegment(sketch, "E255", {"start": v(-7.57, -189.9) * mm, "end": v(-7.14, -189.15) * mm});
            skArc(sketch, "E256", {"start": v(-7.14, -189.15) * mm, "mid": v(-7.12, -189.1) * mm, "end": v(-7.11, -189.05) * mm});
            skLineSegment(sketch, "E257", {"start": v(-7.11, -189.05) * mm, "end": v(-7.11, -186.77) * mm});
            skArc(sketch, "E258", {"start": v(-6.96, -186.41) * mm, "mid": v(-7.07, -186.58) * mm, "end": v(-7.11, -186.77) * mm});
            skLineSegment(sketch, "E259", {"start": v(-6.96, -186.41) * mm, "end": v(-4.7, -184.15) * mm});
            skArc(sketch, "E260", {"start": v(-4.34, -184) * mm, "mid": v(-4.53, -184.04) * mm, "end": v(-4.7, -184.15) * mm});
            skLineSegment(sketch, "E261", {"start": v(-4.34, -184) * mm, "end": v(-3.61, -184) * mm});
            skArc(sketch, "E262", {"start": v(-3.11, -184.5) * mm, "mid": v(-3.26, -184.15) * mm, "end": v(-3.61, -184) * mm});
            skLineSegment(sketch, "E263", {"start": v(-3.11, -184.5) * mm, "end": v(-3.11, -186.5) * mm});
            skArc(sketch, "E264", {"start": v(-3.11, -186.5) * mm, "mid": v(-2.96, -186.85) * mm, "end": v(-2.61, -187) * mm});
            skLineSegment(sketch, "E265", {"start": v(-2.61, -187) * mm, "end": v(-2.31, -187) * mm});
            skArc(sketch, "E266", {"start": v(-2.31, -187) * mm, "mid": v(-2.17, -186.94) * mm, "end": v(-2.11, -186.8) * mm});
            skLineSegment(sketch, "E267", {"start": v(-2.11, -186.8) * mm, "end": v(-2.11, -186.65) * mm});
            skArc(sketch, "E268", {"start": v(-1.91, -186.45) * mm, "mid": v(-2.05, -186.5) * mm, "end": v(-2.11, -186.65) * mm});
            skLineSegment(sketch, "E269", {"start": v(-1.91, -186.45) * mm, "end": v(-1.81, -186.45) * mm});
            skArc(sketch, "E270", {"start": v(-1.81, -186.45) * mm, "mid": v(-1.67, -186.4) * mm, "end": v(-1.61, -186.25) * mm});
            skLineSegment(sketch, "E271", {"start": v(-1.61, -186.25) * mm, "end": v(-1.61, -181.5) * mm});
            skArc(sketch, "E272", {"start": v(-1.61, -181.5) * mm, "mid": v(-2.05, -180.44) * mm, "end": v(-3.11, -180) * mm});
            skLineSegment(sketch, "E273", {"start": v(-3.11, -180) * mm, "end": v(-7.86, -180) * mm});
            skArc(sketch, "E274", {"start": v(-7.86, -180) * mm, "mid": v(-8, -180.06) * mm, "end": v(-8.06, -180.2) * mm});
            skLineSegment(sketch, "E275", {"start": v(-8.06, -180.2) * mm, "end": v(-8.06, -180.3) * mm});
            skArc(sketch, "E276", {"start": v(-8.26, -180.5) * mm, "mid": v(-8.12, -180.44) * mm, "end": v(-8.06, -180.3) * mm});
            skLineSegment(sketch, "E277", {"start": v(-8.26, -180.5) * mm, "end": v(-8.41, -180.5) * mm});
            skArc(sketch, "E278", {"start": v(-8.41, -180.5) * mm, "mid": v(-8.55, -180.56) * mm, "end": v(-8.61, -180.7) * mm});
            skLineSegment(sketch, "E279", {"start": v(-8.61, -180.7) * mm, "end": v(-8.61, -181) * mm});
            skArc(sketch, "E280", {"start": v(-8.61, -181) * mm, "mid": v(-8.46, -181.35) * mm, "end": v(-8.11, -181.5) * mm});
            skLineSegment(sketch, "E281", {"start": v(-8.11, -181.5) * mm, "end": v(-6.11, -181.5) * mm});
            skArc(sketch, "E282", {"start": v(-5.61, -182) * mm, "mid": v(-5.76, -181.65) * mm, "end": v(-6.11, -181.5) * mm});
            skLineSegment(sketch, "E283", {"start": v(-5.61, -182) * mm, "end": v(-5.61, -182.73) * mm});
            skArc(sketch, "E284", {"start": v(-5.76, -183.09) * mm, "mid": v(-5.65, -182.92) * mm, "end": v(-5.61, -182.73) * mm});
            skLineSegment(sketch, "E285", {"start": v(-5.76, -183.09) * mm, "end": v(-8.03, -185.35) * mm});
            skArc(sketch, "E286", {"start": v(-8.38, -185.5) * mm, "mid": v(-8.19, -185.46) * mm, "end": v(-8.03, -185.35) * mm});
            skLineSegment(sketch, "E287", {"start": v(-8.38, -185.5) * mm, "end": v(-10.66, -185.5) * mm});
            skArc(sketch, "E288", {"start": v(-10.66, -185.5) * mm, "mid": v(-10.7, -185.5) * mm, "end": v(-10.76, -185.53) * mm});
            skLineSegment(sketch, "E289", {"start": v(-10.76, -185.53) * mm, "end": v(-11.51, -185.96) * mm});
            skArc(sketch, "E290", {"start": v(-11.71, -185.96) * mm, "mid": v(-11.61, -185.99) * mm, "end": v(-11.51, -185.96) * mm});
            skLineSegment(sketch, "E291", {"start": v(-11.71, -185.96) * mm, "end": v(-12.46, -185.53) * mm});
            skArc(sketch, "E292", {"start": v(-12.46, -185.53) * mm, "mid": v(-12.51, -185.5) * mm, "end": v(-12.56, -185.5) * mm});
            skLineSegment(sketch, "E293", {"start": v(-12.56, -185.5) * mm, "end": v(-14.84, -185.5) * mm});
            skArc(sketch, "E294", {"start": v(-15.2, -185.35) * mm, "mid": v(-15.03, -185.46) * mm, "end": v(-14.84, -185.5) * mm});
            skLineSegment(sketch, "E295", {"start": v(-15.2, -185.35) * mm, "end": v(-17.46, -183.09) * mm});
            skArc(sketch, "E296", {"start": v(-17.61, -182.73) * mm, "mid": v(-17.57, -182.92) * mm, "end": v(-17.46, -183.09) * mm});
            skLineSegment(sketch, "E297", {"start": v(-17.61, -182.73) * mm, "end": v(-17.61, -182) * mm});
            skArc(sketch, "E298", {"start": v(-17.11, -181.5) * mm, "mid": v(-17.46, -181.65) * mm, "end": v(-17.61, -182) * mm});
            skLineSegment(sketch, "E299", {"start": v(-17.11, -181.5) * mm, "end": v(-15.11, -181.5) * mm});
            skArc(sketch, "E300", {"start": v(-15.11, -181.5) * mm, "mid": v(-14.76, -181.35) * mm, "end": v(-14.61, -181) * mm});
            skLineSegment(sketch, "E301", {"start": v(-14.61, -181) * mm, "end": v(-14.61, -180.7) * mm});
            skArc(sketch, "E302", {"start": v(-14.61, -180.7) * mm, "mid": v(-14.67, -180.56) * mm, "end": v(-14.81, -180.5) * mm});
            skLineSegment(sketch, "E303", {"start": v(-14.81, -180.5) * mm, "end": v(-14.96, -180.5) * mm});
            skArc(sketch, "E304", {"start": v(-15.16, -180.3) * mm, "mid": v(-15.1, -180.44) * mm, "end": v(-14.96, -180.5) * mm});
            skLineSegment(sketch, "E305", {"start": v(-15.16, -180.3) * mm, "end": v(-15.16, -180.2) * mm});
            skArc(sketch, "E306", {"start": v(-15.16, -180.2) * mm, "mid": v(-15.22, -180.06) * mm, "end": v(-15.36, -180) * mm});
            skLineSegment(sketch, "E307", {"start": v(-15.36, -180) * mm, "end": v(-20.11, -180) * mm});
            skArc(sketch, "E308", {"start": v(-13.52, -187.01) * mm, "mid": v(-14.12, -187.5) * mm, "end": v(-14.6, -188.1) * mm});
            skLineSegment(sketch, "E309", {"start": v(-12.87, -187.55) * mm, "end": v(-13.52, -187.01) * mm});
            skArc(sketch, "E310", {"start": v(-10.35, -187.55) * mm, "mid": v(-11.61, -187.25) * mm, "end": v(-12.87, -187.55) * mm});
            skLineSegment(sketch, "E311", {"start": v(-9.7, -187.01) * mm, "end": v(-10.35, -187.55) * mm});
            skArc(sketch, "E312", {"start": v(-8.62, -188.1) * mm, "mid": v(-9.1, -187.5) * mm, "end": v(-9.7, -187.01) * mm});
            skLineSegment(sketch, "E313", {"start": v(-9.17, -188.74) * mm, "end": v(-8.62, -188.1) * mm});
            skArc(sketch, "E314", {"start": v(-9.17, -191.26) * mm, "mid": v(-8.86, -190) * mm, "end": v(-9.17, -188.74) * mm});
            skLineSegment(sketch, "E315", {"start": v(-8.62, -191.9) * mm, "end": v(-9.17, -191.26) * mm});
            skArc(sketch, "E316", {"start": v(-9.7, -192.99) * mm, "mid": v(-9.1, -192.5) * mm, "end": v(-8.62, -191.9) * mm});
            skLineSegment(sketch, "E317", {"start": v(-10.35, -192.45) * mm, "end": v(-9.7, -192.99) * mm});
            skArc(sketch, "E318", {"start": v(-12.87, -192.45) * mm, "mid": v(-11.61, -192.75) * mm, "end": v(-10.35, -192.45) * mm});
            skLineSegment(sketch, "E319", {"start": v(-13.52, -192.99) * mm, "end": v(-12.87, -192.45) * mm});
            skArc(sketch, "E320", {"start": v(-14.6, -191.9) * mm, "mid": v(-14.12, -192.5) * mm, "end": v(-13.52, -192.99) * mm});
            skLineSegment(sketch, "E321", {"start": v(-14.06, -191.26) * mm, "end": v(-14.6, -191.9) * mm});
            skArc(sketch, "E322", {"start": v(-14.06, -188.74) * mm, "mid": v(-14.36, -190) * mm, "end": v(-14.06, -191.26) * mm});
            skLineSegment(sketch, "E323", {"start": v(-14.6, -188.1) * mm, "end": v(-14.06, -188.74) * mm});
            skSolve(sketch);
        }
        {
            var Q0;
            Q0=makeQuery(id+"F9.imprint","IMPRINT",FACE,{"disambiguationData":[TD([[makeQuery(id+"F9.imprint","IMPRINT",EDGE,{"derivedFrom":sQuery(id+"F9.wireOp",EDGE,"E164")}),1.0]])]});
            var Q1;
            Q1=makeQuery(id+"F9.imprint","IMPRINT",FACE,{"disambiguationData":[TD([[makeQuery(id+"F9.imprint","IMPRINT",EDGE,{"derivedFrom":sQuery(id+"F9.wireOp",EDGE,"E308")}),1.0]])]});
            var Q2;
            Q2=makeQuery(id+"F9.imprint","IMPRINT",FACE,{"disambiguationData":[TD([[makeQuery(id+"F9.imprint","IMPRINT",EDGE,{"derivedFrom":sQuery(id+"F9.wireOp",EDGE,"E148")}),1.0]])]});
            var Q3;
            Q3=makeQuery(id+"F9.imprint","IMPRINT",FACE,{"disambiguationData":[TD([[makeQuery(id+"F9.imprint","IMPRINT",EDGE,{"derivedFrom":sQuery(id+"F9.wireOp",EDGE,"E4")}),1.0]])]});
            extrude(context, id + "F10", {"entities" : qUnion([Q0, Q1, Q2, Q3]), "oppositeDirection" : true, "depth" : 1150 * mm, "offsetDistance" : 25 * mm, "hasSecondDirection" : true, "secondDirectionOppositeDirection" : false, "secondDirectionDepth" : 550 * mm});
        }
        {
            var Q0;
            Q0=makeQuery(id+"F6.opPattern","COPY",FACE,{"derivedFrom":makeQuery(id+"F1.opExtrude","CAP_FACE",FACE,{"disambiguationData":[OSD([sQuery(id+"F0.wireOp",EDGE,"E0.bottom"),sQuery(id+"F0.wireOp",EDGE,"E0.top"),sQuery(id+"F0.wireOp",EDGE,"E0.left"),sQuery(id+"F0.wireOp",EDGE,"E0.right")])],"isStart":false}),"instanceName":"1"});
            var sketch = newSketch(context, id + "F11", { "sketchPlane" : qUnion([Q0])});
            skArc(sketch, "E324", {"start": v(-296.64, 220.6) * mm, "mid": v(-297.7, 220.16) * mm, "end": v(-298.14, 219.1) * mm});
            skLineSegment(sketch, "E325", {"start": v(-298.14, 219.1) * mm, "end": v(-298.14, 214.35) * mm});
            skArc(sketch, "E326", {"start": v(-298.14, 214.35) * mm, "mid": v(-298.08, 214.2) * mm, "end": v(-297.94, 214.15) * mm});
            skLineSegment(sketch, "E327", {"start": v(-297.94, 214.15) * mm, "end": v(-297.84, 214.15) * mm});
            skArc(sketch, "E328", {"start": v(-297.64, 213.95) * mm, "mid": v(-297.7, 214.1) * mm, "end": v(-297.84, 214.15) * mm});
            skLineSegment(sketch, "E329", {"start": v(-297.64, 213.95) * mm, "end": v(-297.64, 213.8) * mm});
            skArc(sketch, "E330", {"start": v(-297.64, 213.8) * mm, "mid": v(-297.58, 213.66) * mm, "end": v(-297.44, 213.6) * mm});
            skLineSegment(sketch, "E331", {"start": v(-297.44, 213.6) * mm, "end": v(-297.14, 213.6) * mm});
            skArc(sketch, "E332", {"start": v(-297.14, 213.6) * mm, "mid": v(-296.78, 213.75) * mm, "end": v(-296.64, 214.1) * mm});
            skLineSegment(sketch, "E333", {"start": v(-296.64, 214.1) * mm, "end": v(-296.64, 216.1) * mm});
            skArc(sketch, "E334", {"start": v(-296.14, 216.6) * mm, "mid": v(-296.5, 216.45) * mm, "end": v(-296.64, 216.1) * mm});
            skLineSegment(sketch, "E335", {"start": v(-296.14, 216.6) * mm, "end": v(-295.4, 216.6) * mm});
            skArc(sketch, "E336", {"start": v(-295.05, 216.45) * mm, "mid": v(-295.21, 216.56) * mm, "end": v(-295.4, 216.6) * mm});
            skLineSegment(sketch, "E337", {"start": v(-295.05, 216.45) * mm, "end": v(-292.78, 214.19) * mm});
            skArc(sketch, "E338", {"start": v(-292.64, 213.83) * mm, "mid": v(-292.67, 214.02) * mm, "end": v(-292.78, 214.19) * mm});
            skLineSegment(sketch, "E339", {"start": v(-292.64, 213.83) * mm, "end": v(-292.64, 211.55) * mm});
            skArc(sketch, "E340", {"start": v(-292.64, 211.55) * mm, "mid": v(-292.63, 211.5) * mm, "end": v(-292.6, 211.45) * mm});
            skLineSegment(sketch, "E341", {"start": v(-292.6, 211.45) * mm, "end": v(-292.17, 210.7) * mm});
            skArc(sketch, "E342", {"start": v(-292.17, 210.5) * mm, "mid": v(-292.15, 210.6) * mm, "end": v(-292.17, 210.7) * mm});
            skLineSegment(sketch, "E343", {"start": v(-292.17, 210.5) * mm, "end": v(-292.6, 209.75) * mm});
            skArc(sketch, "E344", {"start": v(-292.6, 209.75) * mm, "mid": v(-292.63, 209.7) * mm, "end": v(-292.64, 209.65) * mm});
            skLineSegment(sketch, "E345", {"start": v(-292.64, 209.65) * mm, "end": v(-292.64, 207.37) * mm});
            skArc(sketch, "E346", {"start": v(-292.78, 207.01) * mm, "mid": v(-292.67, 207.18) * mm, "end": v(-292.64, 207.37) * mm});
            skLineSegment(sketch, "E347", {"start": v(-292.78, 207.01) * mm, "end": v(-295.05, 204.75) * mm});
            skArc(sketch, "E348", {"start": v(-295.4, 204.6) * mm, "mid": v(-295.21, 204.64) * mm, "end": v(-295.05, 204.75) * mm});
            skLineSegment(sketch, "E349", {"start": v(-295.4, 204.6) * mm, "end": v(-296.14, 204.6) * mm});
            skArc(sketch, "E350", {"start": v(-296.64, 205.1) * mm, "mid": v(-296.5, 204.75) * mm, "end": v(-296.14, 204.6) * mm});
            skLineSegment(sketch, "E351", {"start": v(-296.64, 205.1) * mm, "end": v(-296.64, 207.1) * mm});
            skArc(sketch, "E352", {"start": v(-296.64, 207.1) * mm, "mid": v(-296.78, 207.45) * mm, "end": v(-297.14, 207.6) * mm});
            skLineSegment(sketch, "E353", {"start": v(-297.14, 207.6) * mm, "end": v(-297.44, 207.6) * mm});
            skArc(sketch, "E354", {"start": v(-297.44, 207.6) * mm, "mid": v(-297.58, 207.54) * mm, "end": v(-297.64, 207.4) * mm});
            skLineSegment(sketch, "E355", {"start": v(-297.64, 207.4) * mm, "end": v(-297.64, 207.25) * mm});
            skArc(sketch, "E356", {"start": v(-297.84, 207.05) * mm, "mid": v(-297.7, 207.1) * mm, "end": v(-297.64, 207.25) * mm});
            skLineSegment(sketch, "E357", {"start": v(-297.84, 207.05) * mm, "end": v(-297.94, 207.05) * mm});
            skArc(sketch, "E358", {"start": v(-297.94, 207.05) * mm, "mid": v(-298.08, 207) * mm, "end": v(-298.14, 206.85) * mm});
            skLineSegment(sketch, "E359", {"start": v(-298.14, 206.85) * mm, "end": v(-298.14, 202.1) * mm});
            skArc(sketch, "E360", {"start": v(-298.14, 202.1) * mm, "mid": v(-297.7, 201.04) * mm, "end": v(-296.64, 200.6) * mm});
            skLineSegment(sketch, "E361", {"start": v(-296.64, 200.6) * mm, "end": v(-291.89, 200.6) * mm});
            skArc(sketch, "E362", {"start": v(-291.89, 200.6) * mm, "mid": v(-291.75, 200.66) * mm, "end": v(-291.69, 200.8) * mm});
            skLineSegment(sketch, "E363", {"start": v(-291.69, 200.8) * mm, "end": v(-291.69, 200.9) * mm});
            skArc(sketch, "E364", {"start": v(-291.49, 201.1) * mm, "mid": v(-291.63, 201.04) * mm, "end": v(-291.69, 200.9) * mm});
            skLineSegment(sketch, "E365", {"start": v(-291.49, 201.1) * mm, "end": v(-291.34, 201.1) * mm});
            skArc(sketch, "E366", {"start": v(-291.34, 201.1) * mm, "mid": v(-291.2, 201.16) * mm, "end": v(-291.14, 201.3) * mm});
            skLineSegment(sketch, "E367", {"start": v(-291.14, 201.3) * mm, "end": v(-291.14, 201.6) * mm});
            skArc(sketch, "E368", {"start": v(-291.14, 201.6) * mm, "mid": v(-291.28, 201.95) * mm, "end": v(-291.64, 202.1) * mm});
            skLineSegment(sketch, "E369", {"start": v(-291.64, 202.1) * mm, "end": v(-293.64, 202.1) * mm});
            skArc(sketch, "E370", {"start": v(-294.14, 202.6) * mm, "mid": v(-294, 202.25) * mm, "end": v(-293.64, 202.1) * mm});
            skLineSegment(sketch, "E371", {"start": v(-294.14, 202.6) * mm, "end": v(-294.14, 203.33) * mm});
            skArc(sketch, "E372", {"start": v(-294, 203.69) * mm, "mid": v(-294.1, 203.52) * mm, "end": v(-294.14, 203.33) * mm});
            skLineSegment(sketch, "E373", {"start": v(-294, 203.69) * mm, "end": v(-291.72, 205.95) * mm});
            skArc(sketch, "E374", {"start": v(-291.37, 206.1) * mm, "mid": v(-291.56, 206.06) * mm, "end": v(-291.72, 205.95) * mm});
            skLineSegment(sketch, "E375", {"start": v(-291.37, 206.1) * mm, "end": v(-289.1, 206.1) * mm});
            skArc(sketch, "E376", {"start": v(-289.1, 206.1) * mm, "mid": v(-289.04, 206.1) * mm, "end": v(-289, 206.13) * mm});
            skLineSegment(sketch, "E377", {"start": v(-289, 206.13) * mm, "end": v(-288.24, 206.56) * mm});
            skArc(sketch, "E378", {"start": v(-288.04, 206.56) * mm, "mid": v(-288.14, 206.59) * mm, "end": v(-288.24, 206.56) * mm});
            skLineSegment(sketch, "E379", {"start": v(-288.04, 206.56) * mm, "end": v(-287.28, 206.13) * mm});
            skArc(sketch, "E380", {"start": v(-287.28, 206.13) * mm, "mid": v(-287.23, 206.1) * mm, "end": v(-287.18, 206.1) * mm});
            skLineSegment(sketch, "E381", {"start": v(-287.18, 206.1) * mm, "end": v(-284.9, 206.1) * mm});
            skArc(sketch, "E382", {"start": v(-284.55, 205.95) * mm, "mid": v(-284.71, 206.06) * mm, "end": v(-284.9, 206.1) * mm});
            skLineSegment(sketch, "E383", {"start": v(-284.55, 205.95) * mm, "end": v(-282.28, 203.69) * mm});
            skArc(sketch, "E384", {"start": v(-282.14, 203.33) * mm, "mid": v(-282.17, 203.52) * mm, "end": v(-282.28, 203.69) * mm});
            skLineSegment(sketch, "E385", {"start": v(-282.14, 203.33) * mm, "end": v(-282.14, 202.6) * mm});
            skArc(sketch, "E386", {"start": v(-282.64, 202.1) * mm, "mid": v(-282.28, 202.25) * mm, "end": v(-282.14, 202.6) * mm});
            skLineSegment(sketch, "E387", {"start": v(-282.64, 202.1) * mm, "end": v(-284.64, 202.1) * mm});
            skArc(sketch, "E388", {"start": v(-284.64, 202.1) * mm, "mid": v(-285, 201.95) * mm, "end": v(-285.14, 201.6) * mm});
            skLineSegment(sketch, "E389", {"start": v(-285.14, 201.6) * mm, "end": v(-285.14, 201.3) * mm});
            skArc(sketch, "E390", {"start": v(-285.14, 201.3) * mm, "mid": v(-285.08, 201.16) * mm, "end": v(-284.94, 201.1) * mm});
            skLineSegment(sketch, "E391", {"start": v(-284.94, 201.1) * mm, "end": v(-284.79, 201.1) * mm});
            skArc(sketch, "E392", {"start": v(-284.59, 200.9) * mm, "mid": v(-284.65, 201.04) * mm, "end": v(-284.79, 201.1) * mm});
            skLineSegment(sketch, "E393", {"start": v(-284.59, 200.9) * mm, "end": v(-284.59, 200.8) * mm});
            skArc(sketch, "E394", {"start": v(-284.59, 200.8) * mm, "mid": v(-284.53, 200.66) * mm, "end": v(-284.39, 200.6) * mm});
            skLineSegment(sketch, "E395", {"start": v(-284.39, 200.6) * mm, "end": v(-279.64, 200.6) * mm});
            skArc(sketch, "E396", {"start": v(-279.64, 200.6) * mm, "mid": v(-278.58, 201.04) * mm, "end": v(-278.14, 202.1) * mm});
            skLineSegment(sketch, "E397", {"start": v(-278.14, 202.1) * mm, "end": v(-278.14, 206.85) * mm});
            skArc(sketch, "E398", {"start": v(-278.14, 206.85) * mm, "mid": v(-278.2, 207) * mm, "end": v(-278.34, 207.05) * mm});
            skLineSegment(sketch, "E399", {"start": v(-278.34, 207.05) * mm, "end": v(-278.44, 207.05) * mm});
            skArc(sketch, "E400", {"start": v(-278.64, 207.25) * mm, "mid": v(-278.58, 207.1) * mm, "end": v(-278.44, 207.05) * mm});
            skLineSegment(sketch, "E401", {"start": v(-278.64, 207.25) * mm, "end": v(-278.64, 207.4) * mm});
            skArc(sketch, "E402", {"start": v(-278.64, 207.4) * mm, "mid": v(-278.7, 207.54) * mm, "end": v(-278.84, 207.6) * mm});
            skLineSegment(sketch, "E403", {"start": v(-278.84, 207.6) * mm, "end": v(-279.14, 207.6) * mm});
            skArc(sketch, "E404", {"start": v(-279.14, 207.6) * mm, "mid": v(-279.5, 207.45) * mm, "end": v(-279.64, 207.1) * mm});
            skLineSegment(sketch, "E405", {"start": v(-279.64, 207.1) * mm, "end": v(-279.64, 205.1) * mm});
            skArc(sketch, "E406", {"start": v(-280.14, 204.6) * mm, "mid": v(-279.78, 204.75) * mm, "end": v(-279.64, 205.1) * mm});
            skLineSegment(sketch, "E407", {"start": v(-280.14, 204.6) * mm, "end": v(-280.87, 204.6) * mm});
            skArc(sketch, "E408", {"start": v(-281.22, 204.75) * mm, "mid": v(-281.06, 204.64) * mm, "end": v(-280.87, 204.6) * mm});
            skLineSegment(sketch, "E409", {"start": v(-281.22, 204.75) * mm, "end": v(-283.5, 207.01) * mm});
            skArc(sketch, "E410", {"start": v(-283.64, 207.37) * mm, "mid": v(-283.6, 207.18) * mm, "end": v(-283.5, 207.01) * mm});
            skLineSegment(sketch, "E411", {"start": v(-283.64, 207.37) * mm, "end": v(-283.64, 209.65) * mm});
            skArc(sketch, "E412", {"start": v(-283.64, 209.65) * mm, "mid": v(-283.64, 209.7) * mm, "end": v(-283.66, 209.75) * mm});
            skLineSegment(sketch, "E413", {"start": v(-283.66, 209.75) * mm, "end": v(-284.1, 210.5) * mm});
            skArc(sketch, "E414", {"start": v(-284.1, 210.7) * mm, "mid": v(-284.13, 210.6) * mm, "end": v(-284.1, 210.5) * mm});
            skLineSegment(sketch, "E415", {"start": v(-284.1, 210.7) * mm, "end": v(-283.66, 211.45) * mm});
            skArc(sketch, "E416", {"start": v(-283.66, 211.45) * mm, "mid": v(-283.64, 211.5) * mm, "end": v(-283.64, 211.55) * mm});
            skLineSegment(sketch, "E417", {"start": v(-283.64, 211.55) * mm, "end": v(-283.64, 213.83) * mm});
            skArc(sketch, "E418", {"start": v(-283.5, 214.19) * mm, "mid": v(-283.6, 214.02) * mm, "end": v(-283.64, 213.83) * mm});
            skLineSegment(sketch, "E419", {"start": v(-283.5, 214.19) * mm, "end": v(-281.22, 216.45) * mm});
            skArc(sketch, "E420", {"start": v(-280.87, 216.6) * mm, "mid": v(-281.06, 216.56) * mm, "end": v(-281.22, 216.45) * mm});
            skLineSegment(sketch, "E421", {"start": v(-280.87, 216.6) * mm, "end": v(-280.14, 216.6) * mm});
            skArc(sketch, "E422", {"start": v(-279.64, 216.1) * mm, "mid": v(-279.78, 216.45) * mm, "end": v(-280.14, 216.6) * mm});
            skLineSegment(sketch, "E423", {"start": v(-279.64, 216.1) * mm, "end": v(-279.64, 214.1) * mm});
            skArc(sketch, "E424", {"start": v(-279.64, 214.1) * mm, "mid": v(-279.5, 213.75) * mm, "end": v(-279.14, 213.6) * mm});
            skLineSegment(sketch, "E425", {"start": v(-279.14, 213.6) * mm, "end": v(-278.84, 213.6) * mm});
            skArc(sketch, "E426", {"start": v(-278.84, 213.6) * mm, "mid": v(-278.7, 213.66) * mm, "end": v(-278.64, 213.8) * mm});
            skLineSegment(sketch, "E427", {"start": v(-278.64, 213.8) * mm, "end": v(-278.64, 213.95) * mm});
            skArc(sketch, "E428", {"start": v(-278.44, 214.15) * mm, "mid": v(-278.58, 214.1) * mm, "end": v(-278.64, 213.95) * mm});
            skLineSegment(sketch, "E429", {"start": v(-278.44, 214.15) * mm, "end": v(-278.34, 214.15) * mm});
            skArc(sketch, "E430", {"start": v(-278.34, 214.15) * mm, "mid": v(-278.2, 214.2) * mm, "end": v(-278.14, 214.35) * mm});
            skLineSegment(sketch, "E431", {"start": v(-278.14, 214.35) * mm, "end": v(-278.14, 219.1) * mm});
            skArc(sketch, "E432", {"start": v(-278.14, 219.1) * mm, "mid": v(-278.58, 220.16) * mm, "end": v(-279.64, 220.6) * mm});
            skLineSegment(sketch, "E433", {"start": v(-279.64, 220.6) * mm, "end": v(-284.39, 220.6) * mm});
            skArc(sketch, "E434", {"start": v(-284.39, 220.6) * mm, "mid": v(-284.53, 220.54) * mm, "end": v(-284.59, 220.4) * mm});
            skLineSegment(sketch, "E435", {"start": v(-284.59, 220.4) * mm, "end": v(-284.59, 220.3) * mm});
            skArc(sketch, "E436", {"start": v(-284.79, 220.1) * mm, "mid": v(-284.65, 220.16) * mm, "end": v(-284.59, 220.3) * mm});
            skLineSegment(sketch, "E437", {"start": v(-284.79, 220.1) * mm, "end": v(-284.94, 220.1) * mm});
            skArc(sketch, "E438", {"start": v(-284.94, 220.1) * mm, "mid": v(-285.08, 220.04) * mm, "end": v(-285.14, 219.9) * mm});
            skLineSegment(sketch, "E439", {"start": v(-285.14, 219.9) * mm, "end": v(-285.14, 219.6) * mm});
            skArc(sketch, "E440", {"start": v(-285.14, 219.6) * mm, "mid": v(-285, 219.25) * mm, "end": v(-284.64, 219.1) * mm});
            skLineSegment(sketch, "E441", {"start": v(-284.64, 219.1) * mm, "end": v(-282.64, 219.1) * mm});
            skArc(sketch, "E442", {"start": v(-282.14, 218.6) * mm, "mid": v(-282.28, 218.95) * mm, "end": v(-282.64, 219.1) * mm});
            skLineSegment(sketch, "E443", {"start": v(-282.14, 218.6) * mm, "end": v(-282.14, 217.87) * mm});
            skArc(sketch, "E444", {"start": v(-282.28, 217.51) * mm, "mid": v(-282.17, 217.68) * mm, "end": v(-282.14, 217.87) * mm});
            skLineSegment(sketch, "E445", {"start": v(-282.28, 217.51) * mm, "end": v(-284.55, 215.25) * mm});
            skArc(sketch, "E446", {"start": v(-284.9, 215.1) * mm, "mid": v(-284.71, 215.14) * mm, "end": v(-284.55, 215.25) * mm});
            skLineSegment(sketch, "E447", {"start": v(-284.9, 215.1) * mm, "end": v(-287.18, 215.1) * mm});
            skArc(sketch, "E448", {"start": v(-287.18, 215.1) * mm, "mid": v(-287.23, 215.1) * mm, "end": v(-287.28, 215.07) * mm});
            skLineSegment(sketch, "E449", {"start": v(-287.28, 215.07) * mm, "end": v(-288.04, 214.64) * mm});
            skArc(sketch, "E450", {"start": v(-288.24, 214.64) * mm, "mid": v(-288.14, 214.61) * mm, "end": v(-288.04, 214.64) * mm});
            skLineSegment(sketch, "E451", {"start": v(-288.24, 214.64) * mm, "end": v(-289, 215.07) * mm});
            skArc(sketch, "E452", {"start": v(-289, 215.07) * mm, "mid": v(-289.04, 215.1) * mm, "end": v(-289.1, 215.1) * mm});
            skLineSegment(sketch, "E453", {"start": v(-289.1, 215.1) * mm, "end": v(-291.37, 215.1) * mm});
            skArc(sketch, "E454", {"start": v(-291.72, 215.25) * mm, "mid": v(-291.56, 215.14) * mm, "end": v(-291.37, 215.1) * mm});
            skLineSegment(sketch, "E455", {"start": v(-291.72, 215.25) * mm, "end": v(-294, 217.51) * mm});
            skArc(sketch, "E456", {"start": v(-294.14, 217.87) * mm, "mid": v(-294.1, 217.68) * mm, "end": v(-294, 217.51) * mm});
            skLineSegment(sketch, "E457", {"start": v(-294.14, 217.87) * mm, "end": v(-294.14, 218.6) * mm});
            skArc(sketch, "E458", {"start": v(-293.64, 219.1) * mm, "mid": v(-294, 218.95) * mm, "end": v(-294.14, 218.6) * mm});
            skLineSegment(sketch, "E459", {"start": v(-293.64, 219.1) * mm, "end": v(-291.64, 219.1) * mm});
            skArc(sketch, "E460", {"start": v(-291.64, 219.1) * mm, "mid": v(-291.28, 219.25) * mm, "end": v(-291.14, 219.6) * mm});
            skLineSegment(sketch, "E461", {"start": v(-291.14, 219.6) * mm, "end": v(-291.14, 219.9) * mm});
            skArc(sketch, "E462", {"start": v(-291.14, 219.9) * mm, "mid": v(-291.2, 220.04) * mm, "end": v(-291.34, 220.1) * mm});
            skLineSegment(sketch, "E463", {"start": v(-291.34, 220.1) * mm, "end": v(-291.49, 220.1) * mm});
            skArc(sketch, "E464", {"start": v(-291.69, 220.3) * mm, "mid": v(-291.63, 220.16) * mm, "end": v(-291.49, 220.1) * mm});
            skLineSegment(sketch, "E465", {"start": v(-291.69, 220.3) * mm, "end": v(-291.69, 220.4) * mm});
            skArc(sketch, "E466", {"start": v(-291.69, 220.4) * mm, "mid": v(-291.75, 220.54) * mm, "end": v(-291.89, 220.6) * mm});
            skLineSegment(sketch, "E467", {"start": v(-291.89, 220.6) * mm, "end": v(-296.64, 220.6) * mm});
            skArc(sketch, "E468", {"start": v(-290.05, 213.59) * mm, "mid": v(-290.65, 213.1) * mm, "end": v(-291.13, 212.5) * mm});
            skLineSegment(sketch, "E469", {"start": v(-289.4, 213.05) * mm, "end": v(-290.05, 213.59) * mm});
            skArc(sketch, "E470", {"start": v(-286.88, 213.05) * mm, "mid": v(-288.14, 213.35) * mm, "end": v(-289.4, 213.05) * mm});
            skLineSegment(sketch, "E471", {"start": v(-286.22, 213.59) * mm, "end": v(-286.88, 213.05) * mm});
            skArc(sketch, "E472", {"start": v(-285.14, 212.5) * mm, "mid": v(-285.62, 213.1) * mm, "end": v(-286.22, 213.59) * mm});
            skLineSegment(sketch, "E473", {"start": v(-285.7, 211.86) * mm, "end": v(-285.14, 212.5) * mm});
            skArc(sketch, "E474", {"start": v(-285.7, 209.34) * mm, "mid": v(-285.39, 210.6) * mm, "end": v(-285.7, 211.86) * mm});
            skLineSegment(sketch, "E475", {"start": v(-285.14, 208.7) * mm, "end": v(-285.7, 209.34) * mm});
            skArc(sketch, "E476", {"start": v(-286.22, 207.61) * mm, "mid": v(-285.62, 208.1) * mm, "end": v(-285.14, 208.7) * mm});
            skLineSegment(sketch, "E477", {"start": v(-286.88, 208.15) * mm, "end": v(-286.22, 207.61) * mm});
            skArc(sketch, "E478", {"start": v(-289.4, 208.15) * mm, "mid": v(-288.14, 207.85) * mm, "end": v(-286.88, 208.15) * mm});
            skLineSegment(sketch, "E479", {"start": v(-290.05, 207.61) * mm, "end": v(-289.4, 208.15) * mm});
            skArc(sketch, "E480", {"start": v(-291.13, 208.7) * mm, "mid": v(-290.65, 208.1) * mm, "end": v(-290.05, 207.61) * mm});
            skLineSegment(sketch, "E481", {"start": v(-290.58, 209.34) * mm, "end": v(-291.13, 208.7) * mm});
            skArc(sketch, "E482", {"start": v(-290.58, 211.86) * mm, "mid": v(-290.89, 210.6) * mm, "end": v(-290.58, 209.34) * mm});
            skLineSegment(sketch, "E483", {"start": v(-291.13, 212.5) * mm, "end": v(-290.58, 211.86) * mm});
            skArc(sketch, "E484", {"start": v(-295.16, -200.46) * mm, "mid": v(-296.22, -200.9) * mm, "end": v(-296.66, -201.96) * mm});
            skLineSegment(sketch, "E485", {"start": v(-296.66, -201.96) * mm, "end": v(-296.66, -206.71) * mm});
            skArc(sketch, "E486", {"start": v(-296.66, -206.71) * mm, "mid": v(-296.6, -206.85) * mm, "end": v(-296.46, -206.91) * mm});
            skLineSegment(sketch, "E487", {"start": v(-296.46, -206.91) * mm, "end": v(-296.36, -206.91) * mm});
            skArc(sketch, "E488", {"start": v(-296.16, -207.11) * mm, "mid": v(-296.22, -206.97) * mm, "end": v(-296.36, -206.91) * mm});
            skLineSegment(sketch, "E489", {"start": v(-296.16, -207.11) * mm, "end": v(-296.16, -207.26) * mm});
            skArc(sketch, "E490", {"start": v(-296.16, -207.26) * mm, "mid": v(-296.1, -207.4) * mm, "end": v(-295.96, -207.46) * mm});
            skLineSegment(sketch, "E491", {"start": v(-295.96, -207.46) * mm, "end": v(-295.66, -207.46) * mm});
            skArc(sketch, "E492", {"start": v(-295.66, -207.46) * mm, "mid": v(-295.3, -207.31) * mm, "end": v(-295.16, -206.96) * mm});
            skLineSegment(sketch, "E493", {"start": v(-295.16, -206.96) * mm, "end": v(-295.16, -204.96) * mm});
            skArc(sketch, "E494", {"start": v(-294.66, -204.46) * mm, "mid": v(-295.01, -204.6) * mm, "end": v(-295.16, -204.96) * mm});
            skLineSegment(sketch, "E495", {"start": v(-294.66, -204.46) * mm, "end": v(-293.93, -204.46) * mm});
            skArc(sketch, "E496", {"start": v(-293.57, -204.6) * mm, "mid": v(-293.74, -204.5) * mm, "end": v(-293.93, -204.46) * mm});
            skLineSegment(sketch, "E497", {"start": v(-293.57, -204.6) * mm, "end": v(-291.3, -206.87) * mm});
            skArc(sketch, "E498", {"start": v(-291.16, -207.23) * mm, "mid": v(-291.2, -207.04) * mm, "end": v(-291.3, -206.87) * mm});
            skLineSegment(sketch, "E499", {"start": v(-291.16, -207.23) * mm, "end": v(-291.16, -209.5) * mm});
            skArc(sketch, "E500", {"start": v(-291.16, -209.5) * mm, "mid": v(-291.15, -209.56) * mm, "end": v(-291.13, -209.6) * mm});
            skLineSegment(sketch, "E501", {"start": v(-291.13, -209.6) * mm, "end": v(-290.7, -210.36) * mm});
            skArc(sketch, "E502", {"start": v(-290.7, -210.56) * mm, "mid": v(-290.67, -210.46) * mm, "end": v(-290.7, -210.36) * mm});
            skLineSegment(sketch, "E503", {"start": v(-290.7, -210.56) * mm, "end": v(-291.13, -211.31) * mm});
            skArc(sketch, "E504", {"start": v(-291.13, -211.31) * mm, "mid": v(-291.15, -211.36) * mm, "end": v(-291.16, -211.41) * mm});
            skLineSegment(sketch, "E505", {"start": v(-291.16, -211.41) * mm, "end": v(-291.16, -213.7) * mm});
            skArc(sketch, "E506", {"start": v(-291.3, -214.05) * mm, "mid": v(-291.2, -213.88) * mm, "end": v(-291.16, -213.7) * mm});
            skLineSegment(sketch, "E507", {"start": v(-291.3, -214.05) * mm, "end": v(-293.57, -216.31) * mm});
            skArc(sketch, "E508", {"start": v(-293.93, -216.46) * mm, "mid": v(-293.74, -216.42) * mm, "end": v(-293.57, -216.31) * mm});
            skLineSegment(sketch, "E509", {"start": v(-293.93, -216.46) * mm, "end": v(-294.66, -216.46) * mm});
            skArc(sketch, "E510", {"start": v(-295.16, -215.96) * mm, "mid": v(-295.01, -216.31) * mm, "end": v(-294.66, -216.46) * mm});
            skLineSegment(sketch, "E511", {"start": v(-295.16, -215.96) * mm, "end": v(-295.16, -213.96) * mm});
            skArc(sketch, "E512", {"start": v(-295.16, -213.96) * mm, "mid": v(-295.3, -213.6) * mm, "end": v(-295.66, -213.46) * mm});
            skLineSegment(sketch, "E513", {"start": v(-295.66, -213.46) * mm, "end": v(-295.96, -213.46) * mm});
            skArc(sketch, "E514", {"start": v(-295.96, -213.46) * mm, "mid": v(-296.1, -213.52) * mm, "end": v(-296.16, -213.66) * mm});
            skLineSegment(sketch, "E515", {"start": v(-296.16, -213.66) * mm, "end": v(-296.16, -213.81) * mm});
            skArc(sketch, "E516", {"start": v(-296.36, -214.01) * mm, "mid": v(-296.22, -213.95) * mm, "end": v(-296.16, -213.81) * mm});
            skLineSegment(sketch, "E517", {"start": v(-296.36, -214.01) * mm, "end": v(-296.46, -214.01) * mm});
            skArc(sketch, "E518", {"start": v(-296.46, -214.01) * mm, "mid": v(-296.6, -214.07) * mm, "end": v(-296.66, -214.21) * mm});
            skLineSegment(sketch, "E519", {"start": v(-296.66, -214.21) * mm, "end": v(-296.66, -218.96) * mm});
            skArc(sketch, "E520", {"start": v(-296.66, -218.96) * mm, "mid": v(-296.22, -220.02) * mm, "end": v(-295.16, -220.46) * mm});
            skLineSegment(sketch, "E521", {"start": v(-295.16, -220.46) * mm, "end": v(-290.41, -220.46) * mm});
            skArc(sketch, "E522", {"start": v(-290.41, -220.46) * mm, "mid": v(-290.27, -220.4) * mm, "end": v(-290.21, -220.26) * mm});
            skLineSegment(sketch, "E523", {"start": v(-290.21, -220.26) * mm, "end": v(-290.21, -220.16) * mm});
            skArc(sketch, "E524", {"start": v(-290.01, -219.96) * mm, "mid": v(-290.15, -220.02) * mm, "end": v(-290.21, -220.16) * mm});
            skLineSegment(sketch, "E525", {"start": v(-290.01, -219.96) * mm, "end": v(-289.86, -219.96) * mm});
            skArc(sketch, "E526", {"start": v(-289.86, -219.96) * mm, "mid": v(-289.72, -219.9) * mm, "end": v(-289.66, -219.76) * mm});
            skLineSegment(sketch, "E527", {"start": v(-289.66, -219.76) * mm, "end": v(-289.66, -219.46) * mm});
            skArc(sketch, "E528", {"start": v(-289.66, -219.46) * mm, "mid": v(-289.8, -219.1) * mm, "end": v(-290.16, -218.96) * mm});
            skLineSegment(sketch, "E529", {"start": v(-290.16, -218.96) * mm, "end": v(-292.16, -218.96) * mm});
            skArc(sketch, "E530", {"start": v(-292.66, -218.46) * mm, "mid": v(-292.51, -218.81) * mm, "end": v(-292.16, -218.96) * mm});
            skLineSegment(sketch, "E531", {"start": v(-292.66, -218.46) * mm, "end": v(-292.66, -217.73) * mm});
            skArc(sketch, "E532", {"start": v(-292.51, -217.37) * mm, "mid": v(-292.62, -217.54) * mm, "end": v(-292.66, -217.73) * mm});
            skLineSegment(sketch, "E533", {"start": v(-292.51, -217.37) * mm, "end": v(-290.25, -215.1) * mm});
            skArc(sketch, "E534", {"start": v(-289.9, -214.96) * mm, "mid": v(-290.08, -215) * mm, "end": v(-290.25, -215.1) * mm});
            skLineSegment(sketch, "E535", {"start": v(-289.9, -214.96) * mm, "end": v(-287.61, -214.96) * mm});
            skArc(sketch, "E536", {"start": v(-287.61, -214.96) * mm, "mid": v(-287.56, -214.95) * mm, "end": v(-287.51, -214.93) * mm});
            skLineSegment(sketch, "E537", {"start": v(-287.51, -214.93) * mm, "end": v(-286.76, -214.5) * mm});
            skArc(sketch, "E538", {"start": v(-286.56, -214.5) * mm, "mid": v(-286.66, -214.47) * mm, "end": v(-286.76, -214.5) * mm});
            skLineSegment(sketch, "E539", {"start": v(-286.56, -214.5) * mm, "end": v(-285.8, -214.93) * mm});
            skArc(sketch, "E540", {"start": v(-285.8, -214.93) * mm, "mid": v(-285.76, -214.95) * mm, "end": v(-285.7, -214.96) * mm});
            skLineSegment(sketch, "E541", {"start": v(-285.7, -214.96) * mm, "end": v(-283.43, -214.96) * mm});
            skArc(sketch, "E542", {"start": v(-283.07, -215.1) * mm, "mid": v(-283.24, -215) * mm, "end": v(-283.43, -214.96) * mm});
            skLineSegment(sketch, "E543", {"start": v(-283.07, -215.1) * mm, "end": v(-280.8, -217.37) * mm});
            skArc(sketch, "E544", {"start": v(-280.66, -217.73) * mm, "mid": v(-280.7, -217.54) * mm, "end": v(-280.8, -217.37) * mm});
            skLineSegment(sketch, "E545", {"start": v(-280.66, -217.73) * mm, "end": v(-280.66, -218.46) * mm});
            skArc(sketch, "E546", {"start": v(-281.16, -218.96) * mm, "mid": v(-280.8, -218.81) * mm, "end": v(-280.66, -218.46) * mm});
            skLineSegment(sketch, "E547", {"start": v(-281.16, -218.96) * mm, "end": v(-283.16, -218.96) * mm});
            skArc(sketch, "E548", {"start": v(-283.16, -218.96) * mm, "mid": v(-283.51, -219.1) * mm, "end": v(-283.66, -219.46) * mm});
            skLineSegment(sketch, "E549", {"start": v(-283.66, -219.46) * mm, "end": v(-283.66, -219.76) * mm});
            skArc(sketch, "E550", {"start": v(-283.66, -219.76) * mm, "mid": v(-283.6, -219.9) * mm, "end": v(-283.46, -219.96) * mm});
            skLineSegment(sketch, "E551", {"start": v(-283.46, -219.96) * mm, "end": v(-283.31, -219.96) * mm});
            skArc(sketch, "E552", {"start": v(-283.11, -220.16) * mm, "mid": v(-283.17, -220.02) * mm, "end": v(-283.31, -219.96) * mm});
            skLineSegment(sketch, "E553", {"start": v(-283.11, -220.16) * mm, "end": v(-283.11, -220.26) * mm});
            skArc(sketch, "E554", {"start": v(-283.11, -220.26) * mm, "mid": v(-283.05, -220.4) * mm, "end": v(-282.91, -220.46) * mm});
            skLineSegment(sketch, "E555", {"start": v(-282.91, -220.46) * mm, "end": v(-278.16, -220.46) * mm});
            skArc(sketch, "E556", {"start": v(-278.16, -220.46) * mm, "mid": v(-277.1, -220.02) * mm, "end": v(-276.66, -218.96) * mm});
            skLineSegment(sketch, "E557", {"start": v(-276.66, -218.96) * mm, "end": v(-276.66, -214.21) * mm});
            skArc(sketch, "E558", {"start": v(-276.66, -214.21) * mm, "mid": v(-276.72, -214.07) * mm, "end": v(-276.86, -214.01) * mm});
            skLineSegment(sketch, "E559", {"start": v(-276.86, -214.01) * mm, "end": v(-276.96, -214.01) * mm});
            skArc(sketch, "E560", {"start": v(-277.16, -213.81) * mm, "mid": v(-277.1, -213.95) * mm, "end": v(-276.96, -214.01) * mm});
            skLineSegment(sketch, "E561", {"start": v(-277.16, -213.81) * mm, "end": v(-277.16, -213.66) * mm});
            skArc(sketch, "E562", {"start": v(-277.16, -213.66) * mm, "mid": v(-277.22, -213.52) * mm, "end": v(-277.36, -213.46) * mm});
            skLineSegment(sketch, "E563", {"start": v(-277.36, -213.46) * mm, "end": v(-277.66, -213.46) * mm});
            skArc(sketch, "E564", {"start": v(-277.66, -213.46) * mm, "mid": v(-278.01, -213.6) * mm, "end": v(-278.16, -213.96) * mm});
            skLineSegment(sketch, "E565", {"start": v(-278.16, -213.96) * mm, "end": v(-278.16, -215.96) * mm});
            skArc(sketch, "E566", {"start": v(-278.66, -216.46) * mm, "mid": v(-278.3, -216.31) * mm, "end": v(-278.16, -215.96) * mm});
            skLineSegment(sketch, "E567", {"start": v(-278.66, -216.46) * mm, "end": v(-279.4, -216.46) * mm});
            skArc(sketch, "E568", {"start": v(-279.75, -216.31) * mm, "mid": v(-279.58, -216.42) * mm, "end": v(-279.4, -216.46) * mm});
            skLineSegment(sketch, "E569", {"start": v(-279.75, -216.31) * mm, "end": v(-282.01, -214.05) * mm});
            skArc(sketch, "E570", {"start": v(-282.16, -213.7) * mm, "mid": v(-282.12, -213.88) * mm, "end": v(-282.01, -214.05) * mm});
            skLineSegment(sketch, "E571", {"start": v(-282.16, -213.7) * mm, "end": v(-282.16, -211.41) * mm});
            skArc(sketch, "E572", {"start": v(-282.16, -211.41) * mm, "mid": v(-282.17, -211.36) * mm, "end": v(-282.19, -211.31) * mm});
            skLineSegment(sketch, "E573", {"start": v(-282.19, -211.31) * mm, "end": v(-282.62, -210.56) * mm});
            skArc(sketch, "E574", {"start": v(-282.62, -210.36) * mm, "mid": v(-282.65, -210.46) * mm, "end": v(-282.62, -210.56) * mm});
            skLineSegment(sketch, "E575", {"start": v(-282.62, -210.36) * mm, "end": v(-282.19, -209.6) * mm});
            skArc(sketch, "E576", {"start": v(-282.19, -209.6) * mm, "mid": v(-282.17, -209.56) * mm, "end": v(-282.16, -209.5) * mm});
            skLineSegment(sketch, "E577", {"start": v(-282.16, -209.5) * mm, "end": v(-282.16, -207.23) * mm});
            skArc(sketch, "E578", {"start": v(-282.01, -206.87) * mm, "mid": v(-282.12, -207.04) * mm, "end": v(-282.16, -207.23) * mm});
            skLineSegment(sketch, "E579", {"start": v(-282.01, -206.87) * mm, "end": v(-279.75, -204.6) * mm});
            skArc(sketch, "E580", {"start": v(-279.4, -204.46) * mm, "mid": v(-279.58, -204.5) * mm, "end": v(-279.75, -204.6) * mm});
            skLineSegment(sketch, "E581", {"start": v(-279.4, -204.46) * mm, "end": v(-278.66, -204.46) * mm});
            skArc(sketch, "E582", {"start": v(-278.16, -204.96) * mm, "mid": v(-278.3, -204.6) * mm, "end": v(-278.66, -204.46) * mm});
            skLineSegment(sketch, "E583", {"start": v(-278.16, -204.96) * mm, "end": v(-278.16, -206.96) * mm});
            skArc(sketch, "E584", {"start": v(-278.16, -206.96) * mm, "mid": v(-278.01, -207.31) * mm, "end": v(-277.66, -207.46) * mm});
            skLineSegment(sketch, "E585", {"start": v(-277.66, -207.46) * mm, "end": v(-277.36, -207.46) * mm});
            skArc(sketch, "E586", {"start": v(-277.36, -207.46) * mm, "mid": v(-277.22, -207.4) * mm, "end": v(-277.16, -207.26) * mm});
            skLineSegment(sketch, "E587", {"start": v(-277.16, -207.26) * mm, "end": v(-277.16, -207.11) * mm});
            skArc(sketch, "E588", {"start": v(-276.96, -206.91) * mm, "mid": v(-277.1, -206.97) * mm, "end": v(-277.16, -207.11) * mm});
            skLineSegment(sketch, "E589", {"start": v(-276.96, -206.91) * mm, "end": v(-276.86, -206.91) * mm});
            skArc(sketch, "E590", {"start": v(-276.86, -206.91) * mm, "mid": v(-276.72, -206.85) * mm, "end": v(-276.66, -206.71) * mm});
            skLineSegment(sketch, "E591", {"start": v(-276.66, -206.71) * mm, "end": v(-276.66, -201.96) * mm});
            skArc(sketch, "E592", {"start": v(-276.66, -201.96) * mm, "mid": v(-277.1, -200.9) * mm, "end": v(-278.16, -200.46) * mm});
            skLineSegment(sketch, "E593", {"start": v(-278.16, -200.46) * mm, "end": v(-282.91, -200.46) * mm});
            skArc(sketch, "E594", {"start": v(-282.91, -200.46) * mm, "mid": v(-283.05, -200.52) * mm, "end": v(-283.11, -200.66) * mm});
            skLineSegment(sketch, "E595", {"start": v(-283.11, -200.66) * mm, "end": v(-283.11, -200.76) * mm});
            skArc(sketch, "E596", {"start": v(-283.31, -200.96) * mm, "mid": v(-283.17, -200.9) * mm, "end": v(-283.11, -200.76) * mm});
            skLineSegment(sketch, "E597", {"start": v(-283.31, -200.96) * mm, "end": v(-283.46, -200.96) * mm});
            skArc(sketch, "E598", {"start": v(-283.46, -200.96) * mm, "mid": v(-283.6, -201.02) * mm, "end": v(-283.66, -201.16) * mm});
            skLineSegment(sketch, "E599", {"start": v(-283.66, -201.16) * mm, "end": v(-283.66, -201.46) * mm});
            skArc(sketch, "E600", {"start": v(-283.66, -201.46) * mm, "mid": v(-283.51, -201.81) * mm, "end": v(-283.16, -201.96) * mm});
            skLineSegment(sketch, "E601", {"start": v(-283.16, -201.96) * mm, "end": v(-281.16, -201.96) * mm});
            skArc(sketch, "E602", {"start": v(-280.66, -202.46) * mm, "mid": v(-280.8, -202.1) * mm, "end": v(-281.16, -201.96) * mm});
            skLineSegment(sketch, "E603", {"start": v(-280.66, -202.46) * mm, "end": v(-280.66, -203.2) * mm});
            skArc(sketch, "E604", {"start": v(-280.8, -203.55) * mm, "mid": v(-280.7, -203.38) * mm, "end": v(-280.66, -203.2) * mm});
            skLineSegment(sketch, "E605", {"start": v(-280.8, -203.55) * mm, "end": v(-283.07, -205.81) * mm});
            skArc(sketch, "E606", {"start": v(-283.43, -205.96) * mm, "mid": v(-283.24, -205.92) * mm, "end": v(-283.07, -205.81) * mm});
            skLineSegment(sketch, "E607", {"start": v(-283.43, -205.96) * mm, "end": v(-285.7, -205.96) * mm});
            skArc(sketch, "E608", {"start": v(-285.7, -205.96) * mm, "mid": v(-285.76, -205.97) * mm, "end": v(-285.8, -205.99) * mm});
            skLineSegment(sketch, "E609", {"start": v(-285.8, -205.99) * mm, "end": v(-286.56, -206.42) * mm});
            skArc(sketch, "E610", {"start": v(-286.76, -206.42) * mm, "mid": v(-286.66, -206.45) * mm, "end": v(-286.56, -206.42) * mm});
            skLineSegment(sketch, "E611", {"start": v(-286.76, -206.42) * mm, "end": v(-287.51, -205.99) * mm});
            skArc(sketch, "E612", {"start": v(-287.51, -205.99) * mm, "mid": v(-287.56, -205.97) * mm, "end": v(-287.61, -205.96) * mm});
            skLineSegment(sketch, "E613", {"start": v(-287.61, -205.96) * mm, "end": v(-289.9, -205.96) * mm});
            skArc(sketch, "E614", {"start": v(-290.25, -205.81) * mm, "mid": v(-290.08, -205.92) * mm, "end": v(-289.9, -205.96) * mm});
            skLineSegment(sketch, "E615", {"start": v(-290.25, -205.81) * mm, "end": v(-292.51, -203.55) * mm});
            skArc(sketch, "E616", {"start": v(-292.66, -203.2) * mm, "mid": v(-292.62, -203.38) * mm, "end": v(-292.51, -203.55) * mm});
            skLineSegment(sketch, "E617", {"start": v(-292.66, -203.2) * mm, "end": v(-292.66, -202.46) * mm});
            skArc(sketch, "E618", {"start": v(-292.16, -201.96) * mm, "mid": v(-292.51, -202.1) * mm, "end": v(-292.66, -202.46) * mm});
            skLineSegment(sketch, "E619", {"start": v(-292.16, -201.96) * mm, "end": v(-290.16, -201.96) * mm});
            skArc(sketch, "E620", {"start": v(-290.16, -201.96) * mm, "mid": v(-289.8, -201.81) * mm, "end": v(-289.66, -201.46) * mm});
            skLineSegment(sketch, "E621", {"start": v(-289.66, -201.46) * mm, "end": v(-289.66, -201.16) * mm});
            skArc(sketch, "E622", {"start": v(-289.66, -201.16) * mm, "mid": v(-289.72, -201.02) * mm, "end": v(-289.86, -200.96) * mm});
            skLineSegment(sketch, "E623", {"start": v(-289.86, -200.96) * mm, "end": v(-290.01, -200.96) * mm});
            skArc(sketch, "E624", {"start": v(-290.21, -200.76) * mm, "mid": v(-290.15, -200.9) * mm, "end": v(-290.01, -200.96) * mm});
            skLineSegment(sketch, "E625", {"start": v(-290.21, -200.76) * mm, "end": v(-290.21, -200.66) * mm});
            skArc(sketch, "E626", {"start": v(-290.21, -200.66) * mm, "mid": v(-290.27, -200.52) * mm, "end": v(-290.41, -200.46) * mm});
            skLineSegment(sketch, "E627", {"start": v(-290.41, -200.46) * mm, "end": v(-295.16, -200.46) * mm});
            skArc(sketch, "E628", {"start": v(-288.57, -207.47) * mm, "mid": v(-289.17, -207.95) * mm, "end": v(-289.65, -208.55) * mm});
            skLineSegment(sketch, "E629", {"start": v(-287.92, -208.01) * mm, "end": v(-288.57, -207.47) * mm});
            skArc(sketch, "E630", {"start": v(-285.4, -208.01) * mm, "mid": v(-286.66, -207.71) * mm, "end": v(-287.92, -208.01) * mm});
            skLineSegment(sketch, "E631", {"start": v(-284.75, -207.47) * mm, "end": v(-285.4, -208.01) * mm});
            skArc(sketch, "E632", {"start": v(-283.67, -208.55) * mm, "mid": v(-284.15, -207.95) * mm, "end": v(-284.75, -207.47) * mm});
            skLineSegment(sketch, "E633", {"start": v(-284.22, -209.2) * mm, "end": v(-283.67, -208.55) * mm});
            skArc(sketch, "E634", {"start": v(-284.22, -211.72) * mm, "mid": v(-283.91, -210.46) * mm, "end": v(-284.22, -209.2) * mm});
            skLineSegment(sketch, "E635", {"start": v(-283.67, -212.37) * mm, "end": v(-284.22, -211.72) * mm});
            skArc(sketch, "E636", {"start": v(-284.75, -213.45) * mm, "mid": v(-284.15, -212.97) * mm, "end": v(-283.67, -212.37) * mm});
            skLineSegment(sketch, "E637", {"start": v(-285.4, -212.9) * mm, "end": v(-284.75, -213.45) * mm});
            skArc(sketch, "E638", {"start": v(-287.92, -212.9) * mm, "mid": v(-286.66, -213.21) * mm, "end": v(-285.4, -212.9) * mm});
            skLineSegment(sketch, "E639", {"start": v(-288.57, -213.45) * mm, "end": v(-287.92, -212.9) * mm});
            skArc(sketch, "E640", {"start": v(-289.65, -212.37) * mm, "mid": v(-289.17, -212.97) * mm, "end": v(-288.57, -213.45) * mm});
            skLineSegment(sketch, "E641", {"start": v(-289.1, -211.72) * mm, "end": v(-289.65, -212.37) * mm});
            skArc(sketch, "E642", {"start": v(-289.1, -209.2) * mm, "mid": v(-289.41, -210.46) * mm, "end": v(-289.1, -211.72) * mm});
            skLineSegment(sketch, "E643", {"start": v(-289.65, -208.55) * mm, "end": v(-289.1, -209.2) * mm});
            skArc(sketch, "E644", {"start": v(275.58, -200.26) * mm, "mid": v(274.52, -200.7) * mm, "end": v(274.08, -201.76) * mm});
            skLineSegment(sketch, "E645", {"start": v(274.08, -201.76) * mm, "end": v(274.08, -206.51) * mm});
            skArc(sketch, "E646", {"start": v(274.08, -206.51) * mm, "mid": v(274.14, -206.65) * mm, "end": v(274.28, -206.71) * mm});
            skLineSegment(sketch, "E647", {"start": v(274.28, -206.71) * mm, "end": v(274.38, -206.71) * mm});
            skArc(sketch, "E648", {"start": v(274.58, -206.91) * mm, "mid": v(274.52, -206.77) * mm, "end": v(274.38, -206.71) * mm});
            skLineSegment(sketch, "E649", {"start": v(274.58, -206.91) * mm, "end": v(274.58, -207.06) * mm});
            skArc(sketch, "E650", {"start": v(274.58, -207.06) * mm, "mid": v(274.64, -207.2) * mm, "end": v(274.78, -207.26) * mm});
            skLineSegment(sketch, "E651", {"start": v(274.78, -207.26) * mm, "end": v(275.08, -207.26) * mm});
            skArc(sketch, "E652", {"start": v(275.08, -207.26) * mm, "mid": v(275.43, -207.11) * mm, "end": v(275.58, -206.76) * mm});
            skLineSegment(sketch, "E653", {"start": v(275.58, -206.76) * mm, "end": v(275.58, -204.76) * mm});
            skArc(sketch, "E654", {"start": v(276.08, -204.26) * mm, "mid": v(275.72, -204.4) * mm, "end": v(275.58, -204.76) * mm});
            skLineSegment(sketch, "E655", {"start": v(276.08, -204.26) * mm, "end": v(276.81, -204.26) * mm});
            skArc(sketch, "E656", {"start": v(277.16, -204.4) * mm, "mid": v(277, -204.3) * mm, "end": v(276.81, -204.26) * mm});
            skLineSegment(sketch, "E657", {"start": v(277.16, -204.4) * mm, "end": v(279.43, -206.67) * mm});
            skArc(sketch, "E658", {"start": v(279.58, -207.03) * mm, "mid": v(279.54, -206.84) * mm, "end": v(279.43, -206.67) * mm});
            skLineSegment(sketch, "E659", {"start": v(279.58, -207.03) * mm, "end": v(279.58, -209.3) * mm});
            skArc(sketch, "E660", {"start": v(279.58, -209.3) * mm, "mid": v(279.59, -209.36) * mm, "end": v(279.6, -209.4) * mm});
            skLineSegment(sketch, "E661", {"start": v(279.6, -209.4) * mm, "end": v(280.04, -210.16) * mm});
            skArc(sketch, "E662", {"start": v(280.04, -210.36) * mm, "mid": v(280.07, -210.26) * mm, "end": v(280.04, -210.16) * mm});
            skLineSegment(sketch, "E663", {"start": v(280.04, -210.36) * mm, "end": v(279.6, -211.11) * mm});
            skArc(sketch, "E664", {"start": v(279.6, -211.11) * mm, "mid": v(279.59, -211.16) * mm, "end": v(279.58, -211.21) * mm});
            skLineSegment(sketch, "E665", {"start": v(279.58, -211.21) * mm, "end": v(279.58, -213.5) * mm});
            skArc(sketch, "E666", {"start": v(279.43, -213.85) * mm, "mid": v(279.54, -213.68) * mm, "end": v(279.58, -213.5) * mm});
            skLineSegment(sketch, "E667", {"start": v(279.43, -213.85) * mm, "end": v(277.16, -216.11) * mm});
            skArc(sketch, "E668", {"start": v(276.81, -216.26) * mm, "mid": v(277, -216.22) * mm, "end": v(277.16, -216.11) * mm});
            skLineSegment(sketch, "E669", {"start": v(276.81, -216.26) * mm, "end": v(276.08, -216.26) * mm});
            skArc(sketch, "E670", {"start": v(275.58, -215.76) * mm, "mid": v(275.72, -216.11) * mm, "end": v(276.08, -216.26) * mm});
            skLineSegment(sketch, "E671", {"start": v(275.58, -215.76) * mm, "end": v(275.58, -213.76) * mm});
            skArc(sketch, "E672", {"start": v(275.58, -213.76) * mm, "mid": v(275.43, -213.4) * mm, "end": v(275.08, -213.26) * mm});
            skLineSegment(sketch, "E673", {"start": v(275.08, -213.26) * mm, "end": v(274.78, -213.26) * mm});
            skArc(sketch, "E674", {"start": v(274.78, -213.26) * mm, "mid": v(274.64, -213.32) * mm, "end": v(274.58, -213.46) * mm});
            skLineSegment(sketch, "E675", {"start": v(274.58, -213.46) * mm, "end": v(274.58, -213.61) * mm});
            skArc(sketch, "E676", {"start": v(274.38, -213.81) * mm, "mid": v(274.52, -213.75) * mm, "end": v(274.58, -213.61) * mm});
            skLineSegment(sketch, "E677", {"start": v(274.38, -213.81) * mm, "end": v(274.28, -213.81) * mm});
            skArc(sketch, "E678", {"start": v(274.28, -213.81) * mm, "mid": v(274.14, -213.87) * mm, "end": v(274.08, -214.01) * mm});
            skLineSegment(sketch, "E679", {"start": v(274.08, -214.01) * mm, "end": v(274.08, -218.76) * mm});
            skArc(sketch, "E680", {"start": v(274.08, -218.76) * mm, "mid": v(274.52, -219.82) * mm, "end": v(275.58, -220.26) * mm});
            skLineSegment(sketch, "E681", {"start": v(275.58, -220.26) * mm, "end": v(280.33, -220.26) * mm});
            skArc(sketch, "E682", {"start": v(280.33, -220.26) * mm, "mid": v(280.47, -220.2) * mm, "end": v(280.53, -220.06) * mm});
            skLineSegment(sketch, "E683", {"start": v(280.53, -220.06) * mm, "end": v(280.53, -219.96) * mm});
            skArc(sketch, "E684", {"start": v(280.73, -219.76) * mm, "mid": v(280.59, -219.82) * mm, "end": v(280.53, -219.96) * mm});
            skLineSegment(sketch, "E685", {"start": v(280.73, -219.76) * mm, "end": v(280.88, -219.76) * mm});
            skArc(sketch, "E686", {"start": v(280.88, -219.76) * mm, "mid": v(281.02, -219.7) * mm, "end": v(281.08, -219.56) * mm});
            skLineSegment(sketch, "E687", {"start": v(281.08, -219.56) * mm, "end": v(281.08, -219.26) * mm});
            skArc(sketch, "E688", {"start": v(281.08, -219.26) * mm, "mid": v(280.93, -218.9) * mm, "end": v(280.58, -218.76) * mm});
            skLineSegment(sketch, "E689", {"start": v(280.58, -218.76) * mm, "end": v(278.58, -218.76) * mm});
            skArc(sketch, "E690", {"start": v(278.08, -218.26) * mm, "mid": v(278.22, -218.61) * mm, "end": v(278.58, -218.76) * mm});
            skLineSegment(sketch, "E691", {"start": v(278.08, -218.26) * mm, "end": v(278.08, -217.53) * mm});
            skArc(sketch, "E692", {"start": v(278.22, -217.17) * mm, "mid": v(278.12, -217.34) * mm, "end": v(278.08, -217.53) * mm});
            skLineSegment(sketch, "E693", {"start": v(278.22, -217.17) * mm, "end": v(280.5, -214.9) * mm});
            skArc(sketch, "E694", {"start": v(280.85, -214.76) * mm, "mid": v(280.65, -214.8) * mm, "end": v(280.5, -214.9) * mm});
            skLineSegment(sketch, "E695", {"start": v(280.85, -214.76) * mm, "end": v(283.12, -214.76) * mm});
            skArc(sketch, "E696", {"start": v(283.12, -214.76) * mm, "mid": v(283.18, -214.75) * mm, "end": v(283.22, -214.73) * mm});
            skLineSegment(sketch, "E697", {"start": v(283.22, -214.73) * mm, "end": v(283.98, -214.3) * mm});
            skArc(sketch, "E698", {"start": v(284.18, -214.3) * mm, "mid": v(284.08, -214.27) * mm, "end": v(283.98, -214.3) * mm});
            skLineSegment(sketch, "E699", {"start": v(284.18, -214.3) * mm, "end": v(284.93, -214.73) * mm});
            skArc(sketch, "E700", {"start": v(284.93, -214.73) * mm, "mid": v(284.98, -214.75) * mm, "end": v(285.03, -214.76) * mm});
            skLineSegment(sketch, "E701", {"start": v(285.03, -214.76) * mm, "end": v(287.31, -214.76) * mm});
            skArc(sketch, "E702", {"start": v(287.66, -214.9) * mm, "mid": v(287.5, -214.8) * mm, "end": v(287.31, -214.76) * mm});
            skLineSegment(sketch, "E703", {"start": v(287.66, -214.9) * mm, "end": v(289.93, -217.17) * mm});
            skArc(sketch, "E704", {"start": v(290.08, -217.53) * mm, "mid": v(290.04, -217.34) * mm, "end": v(289.93, -217.17) * mm});
            skLineSegment(sketch, "E705", {"start": v(290.08, -217.53) * mm, "end": v(290.08, -218.26) * mm});
            skArc(sketch, "E706", {"start": v(289.58, -218.76) * mm, "mid": v(289.93, -218.61) * mm, "end": v(290.08, -218.26) * mm});
            skLineSegment(sketch, "E707", {"start": v(289.58, -218.76) * mm, "end": v(287.58, -218.76) * mm});
            skArc(sketch, "E708", {"start": v(287.58, -218.76) * mm, "mid": v(287.22, -218.9) * mm, "end": v(287.08, -219.26) * mm});
            skLineSegment(sketch, "E709", {"start": v(287.08, -219.26) * mm, "end": v(287.08, -219.56) * mm});
            skArc(sketch, "E710", {"start": v(287.08, -219.56) * mm, "mid": v(287.14, -219.7) * mm, "end": v(287.28, -219.76) * mm});
            skLineSegment(sketch, "E711", {"start": v(287.28, -219.76) * mm, "end": v(287.43, -219.76) * mm});
            skArc(sketch, "E712", {"start": v(287.63, -219.96) * mm, "mid": v(287.57, -219.82) * mm, "end": v(287.43, -219.76) * mm});
            skLineSegment(sketch, "E713", {"start": v(287.63, -219.96) * mm, "end": v(287.63, -220.06) * mm});
            skArc(sketch, "E714", {"start": v(287.63, -220.06) * mm, "mid": v(287.69, -220.2) * mm, "end": v(287.83, -220.26) * mm});
            skLineSegment(sketch, "E715", {"start": v(287.83, -220.26) * mm, "end": v(292.58, -220.26) * mm});
            skArc(sketch, "E716", {"start": v(292.58, -220.26) * mm, "mid": v(293.64, -219.82) * mm, "end": v(294.08, -218.76) * mm});
            skLineSegment(sketch, "E717", {"start": v(294.08, -218.76) * mm, "end": v(294.08, -214.01) * mm});
            skArc(sketch, "E718", {"start": v(294.08, -214.01) * mm, "mid": v(294.02, -213.87) * mm, "end": v(293.88, -213.81) * mm});
            skLineSegment(sketch, "E719", {"start": v(293.88, -213.81) * mm, "end": v(293.78, -213.81) * mm});
            skArc(sketch, "E720", {"start": v(293.58, -213.61) * mm, "mid": v(293.64, -213.75) * mm, "end": v(293.78, -213.81) * mm});
            skLineSegment(sketch, "E721", {"start": v(293.58, -213.61) * mm, "end": v(293.58, -213.46) * mm});
            skArc(sketch, "E722", {"start": v(293.58, -213.46) * mm, "mid": v(293.52, -213.32) * mm, "end": v(293.38, -213.26) * mm});
            skLineSegment(sketch, "E723", {"start": v(293.38, -213.26) * mm, "end": v(293.08, -213.26) * mm});
            skArc(sketch, "E724", {"start": v(293.08, -213.26) * mm, "mid": v(292.72, -213.4) * mm, "end": v(292.58, -213.76) * mm});
            skLineSegment(sketch, "E725", {"start": v(292.58, -213.76) * mm, "end": v(292.58, -215.76) * mm});
            skArc(sketch, "E726", {"start": v(292.08, -216.26) * mm, "mid": v(292.43, -216.11) * mm, "end": v(292.58, -215.76) * mm});
            skLineSegment(sketch, "E727", {"start": v(292.08, -216.26) * mm, "end": v(291.35, -216.26) * mm});
            skArc(sketch, "E728", {"start": v(291, -216.11) * mm, "mid": v(291.15, -216.22) * mm, "end": v(291.35, -216.26) * mm});
            skLineSegment(sketch, "E729", {"start": v(291, -216.11) * mm, "end": v(288.72, -213.85) * mm});
            skArc(sketch, "E730", {"start": v(288.58, -213.5) * mm, "mid": v(288.62, -213.68) * mm, "end": v(288.72, -213.85) * mm});
            skLineSegment(sketch, "E731", {"start": v(288.58, -213.5) * mm, "end": v(288.58, -211.21) * mm});
            skArc(sketch, "E732", {"start": v(288.58, -211.21) * mm, "mid": v(288.57, -211.16) * mm, "end": v(288.55, -211.11) * mm});
            skLineSegment(sketch, "E733", {"start": v(288.55, -211.11) * mm, "end": v(288.12, -210.36) * mm});
            skArc(sketch, "E734", {"start": v(288.12, -210.16) * mm, "mid": v(288.09, -210.26) * mm, "end": v(288.12, -210.36) * mm});
            skLineSegment(sketch, "E735", {"start": v(288.12, -210.16) * mm, "end": v(288.55, -209.4) * mm});
            skArc(sketch, "E736", {"start": v(288.55, -209.4) * mm, "mid": v(288.57, -209.36) * mm, "end": v(288.58, -209.3) * mm});
            skLineSegment(sketch, "E737", {"start": v(288.58, -209.3) * mm, "end": v(288.58, -207.03) * mm});
            skArc(sketch, "E738", {"start": v(288.72, -206.67) * mm, "mid": v(288.62, -206.84) * mm, "end": v(288.58, -207.03) * mm});
            skLineSegment(sketch, "E739", {"start": v(288.72, -206.67) * mm, "end": v(291, -204.4) * mm});
            skArc(sketch, "E740", {"start": v(291.35, -204.26) * mm, "mid": v(291.15, -204.3) * mm, "end": v(291, -204.4) * mm});
            skLineSegment(sketch, "E741", {"start": v(291.35, -204.26) * mm, "end": v(292.08, -204.26) * mm});
            skArc(sketch, "E742", {"start": v(292.58, -204.76) * mm, "mid": v(292.43, -204.4) * mm, "end": v(292.08, -204.26) * mm});
            skLineSegment(sketch, "E743", {"start": v(292.58, -204.76) * mm, "end": v(292.58, -206.76) * mm});
            skArc(sketch, "E744", {"start": v(292.58, -206.76) * mm, "mid": v(292.72, -207.11) * mm, "end": v(293.08, -207.26) * mm});
            skLineSegment(sketch, "E745", {"start": v(293.08, -207.26) * mm, "end": v(293.38, -207.26) * mm});
            skArc(sketch, "E746", {"start": v(293.38, -207.26) * mm, "mid": v(293.52, -207.2) * mm, "end": v(293.58, -207.06) * mm});
            skLineSegment(sketch, "E747", {"start": v(293.58, -207.06) * mm, "end": v(293.58, -206.91) * mm});
            skArc(sketch, "E748", {"start": v(293.78, -206.71) * mm, "mid": v(293.64, -206.77) * mm, "end": v(293.58, -206.91) * mm});
            skLineSegment(sketch, "E749", {"start": v(293.78, -206.71) * mm, "end": v(293.88, -206.71) * mm});
            skArc(sketch, "E750", {"start": v(293.88, -206.71) * mm, "mid": v(294.02, -206.65) * mm, "end": v(294.08, -206.51) * mm});
            skLineSegment(sketch, "E751", {"start": v(294.08, -206.51) * mm, "end": v(294.08, -201.76) * mm});
            skArc(sketch, "E752", {"start": v(294.08, -201.76) * mm, "mid": v(293.64, -200.7) * mm, "end": v(292.58, -200.26) * mm});
            skLineSegment(sketch, "E753", {"start": v(292.58, -200.26) * mm, "end": v(287.83, -200.26) * mm});
            skArc(sketch, "E754", {"start": v(287.83, -200.26) * mm, "mid": v(287.69, -200.32) * mm, "end": v(287.63, -200.46) * mm});
            skLineSegment(sketch, "E755", {"start": v(287.63, -200.46) * mm, "end": v(287.63, -200.56) * mm});
            skArc(sketch, "E756", {"start": v(287.43, -200.76) * mm, "mid": v(287.57, -200.7) * mm, "end": v(287.63, -200.56) * mm});
            skLineSegment(sketch, "E757", {"start": v(287.43, -200.76) * mm, "end": v(287.28, -200.76) * mm});
            skArc(sketch, "E758", {"start": v(287.28, -200.76) * mm, "mid": v(287.14, -200.82) * mm, "end": v(287.08, -200.96) * mm});
            skLineSegment(sketch, "E759", {"start": v(287.08, -200.96) * mm, "end": v(287.08, -201.26) * mm});
            skArc(sketch, "E760", {"start": v(287.08, -201.26) * mm, "mid": v(287.22, -201.61) * mm, "end": v(287.58, -201.76) * mm});
            skLineSegment(sketch, "E761", {"start": v(287.58, -201.76) * mm, "end": v(289.58, -201.76) * mm});
            skArc(sketch, "E762", {"start": v(290.08, -202.26) * mm, "mid": v(289.93, -201.9) * mm, "end": v(289.58, -201.76) * mm});
            skLineSegment(sketch, "E763", {"start": v(290.08, -202.26) * mm, "end": v(290.08, -203) * mm});
            skArc(sketch, "E764", {"start": v(289.93, -203.35) * mm, "mid": v(290.04, -203.18) * mm, "end": v(290.08, -203) * mm});
            skLineSegment(sketch, "E765", {"start": v(289.93, -203.35) * mm, "end": v(287.66, -205.61) * mm});
            skArc(sketch, "E766", {"start": v(287.31, -205.76) * mm, "mid": v(287.5, -205.72) * mm, "end": v(287.66, -205.61) * mm});
            skLineSegment(sketch, "E767", {"start": v(287.31, -205.76) * mm, "end": v(285.03, -205.76) * mm});
            skArc(sketch, "E768", {"start": v(285.03, -205.76) * mm, "mid": v(284.98, -205.77) * mm, "end": v(284.93, -205.79) * mm});
            skLineSegment(sketch, "E769", {"start": v(284.93, -205.79) * mm, "end": v(284.18, -206.22) * mm});
            skArc(sketch, "E770", {"start": v(283.98, -206.22) * mm, "mid": v(284.08, -206.25) * mm, "end": v(284.18, -206.22) * mm});
            skLineSegment(sketch, "E771", {"start": v(283.98, -206.22) * mm, "end": v(283.22, -205.79) * mm});
            skArc(sketch, "E772", {"start": v(283.22, -205.79) * mm, "mid": v(283.18, -205.77) * mm, "end": v(283.12, -205.76) * mm});
            skLineSegment(sketch, "E773", {"start": v(283.12, -205.76) * mm, "end": v(280.85, -205.76) * mm});
            skArc(sketch, "E774", {"start": v(280.5, -205.61) * mm, "mid": v(280.65, -205.72) * mm, "end": v(280.85, -205.76) * mm});
            skLineSegment(sketch, "E775", {"start": v(280.5, -205.61) * mm, "end": v(278.22, -203.35) * mm});
            skArc(sketch, "E776", {"start": v(278.08, -203) * mm, "mid": v(278.12, -203.18) * mm, "end": v(278.22, -203.35) * mm});
            skLineSegment(sketch, "E777", {"start": v(278.08, -203) * mm, "end": v(278.08, -202.26) * mm});
            skArc(sketch, "E778", {"start": v(278.58, -201.76) * mm, "mid": v(278.22, -201.9) * mm, "end": v(278.08, -202.26) * mm});
            skLineSegment(sketch, "E779", {"start": v(278.58, -201.76) * mm, "end": v(280.58, -201.76) * mm});
            skArc(sketch, "E780", {"start": v(280.58, -201.76) * mm, "mid": v(280.93, -201.61) * mm, "end": v(281.08, -201.26) * mm});
            skLineSegment(sketch, "E781", {"start": v(281.08, -201.26) * mm, "end": v(281.08, -200.96) * mm});
            skArc(sketch, "E782", {"start": v(281.08, -200.96) * mm, "mid": v(281.02, -200.82) * mm, "end": v(280.88, -200.76) * mm});
            skLineSegment(sketch, "E783", {"start": v(280.88, -200.76) * mm, "end": v(280.73, -200.76) * mm});
            skArc(sketch, "E784", {"start": v(280.53, -200.56) * mm, "mid": v(280.59, -200.7) * mm, "end": v(280.73, -200.76) * mm});
            skLineSegment(sketch, "E785", {"start": v(280.53, -200.56) * mm, "end": v(280.53, -200.46) * mm});
            skArc(sketch, "E786", {"start": v(280.53, -200.46) * mm, "mid": v(280.47, -200.32) * mm, "end": v(280.33, -200.26) * mm});
            skLineSegment(sketch, "E787", {"start": v(280.33, -200.26) * mm, "end": v(275.58, -200.26) * mm});
            skArc(sketch, "E788", {"start": v(282.16, -207.27) * mm, "mid": v(281.57, -207.75) * mm, "end": v(281.09, -208.35) * mm});
            skLineSegment(sketch, "E789", {"start": v(282.82, -207.81) * mm, "end": v(282.16, -207.27) * mm});
            skArc(sketch, "E790", {"start": v(285.34, -207.81) * mm, "mid": v(284.08, -207.51) * mm, "end": v(282.82, -207.81) * mm});
            skLineSegment(sketch, "E791", {"start": v(286, -207.27) * mm, "end": v(285.34, -207.81) * mm});
            skArc(sketch, "E792", {"start": v(287.07, -208.35) * mm, "mid": v(286.59, -207.75) * mm, "end": v(286, -207.27) * mm});
            skLineSegment(sketch, "E793", {"start": v(286.52, -209) * mm, "end": v(287.07, -208.35) * mm});
            skArc(sketch, "E794", {"start": v(286.52, -211.52) * mm, "mid": v(286.83, -210.26) * mm, "end": v(286.52, -209) * mm});
            skLineSegment(sketch, "E795", {"start": v(287.07, -212.17) * mm, "end": v(286.52, -211.52) * mm});
            skArc(sketch, "E796", {"start": v(286, -213.25) * mm, "mid": v(286.59, -212.77) * mm, "end": v(287.07, -212.17) * mm});
            skLineSegment(sketch, "E797", {"start": v(285.34, -212.7) * mm, "end": v(286, -213.25) * mm});
            skArc(sketch, "E798", {"start": v(282.82, -212.7) * mm, "mid": v(284.08, -213.01) * mm, "end": v(285.34, -212.7) * mm});
            skLineSegment(sketch, "E799", {"start": v(282.16, -213.25) * mm, "end": v(282.82, -212.7) * mm});
            skArc(sketch, "E800", {"start": v(281.09, -212.17) * mm, "mid": v(281.57, -212.77) * mm, "end": v(282.16, -213.25) * mm});
            skLineSegment(sketch, "E801", {"start": v(281.63, -211.52) * mm, "end": v(281.09, -212.17) * mm});
            skArc(sketch, "E802", {"start": v(281.63, -209) * mm, "mid": v(281.33, -210.26) * mm, "end": v(281.63, -211.52) * mm});
            skLineSegment(sketch, "E803", {"start": v(281.09, -208.35) * mm, "end": v(281.63, -209) * mm});
            skArc(sketch, "E804", {"start": v(280.53, 221.1) * mm, "mid": v(279.47, 220.66) * mm, "end": v(279.03, 219.6) * mm});
            skLineSegment(sketch, "E805", {"start": v(279.03, 219.6) * mm, "end": v(279.03, 214.85) * mm});
            skArc(sketch, "E806", {"start": v(279.03, 214.85) * mm, "mid": v(279.09, 214.7) * mm, "end": v(279.23, 214.65) * mm});
            skLineSegment(sketch, "E807", {"start": v(279.23, 214.65) * mm, "end": v(279.33, 214.65) * mm});
            skArc(sketch, "E808", {"start": v(279.53, 214.45) * mm, "mid": v(279.47, 214.6) * mm, "end": v(279.33, 214.65) * mm});
            skLineSegment(sketch, "E809", {"start": v(279.53, 214.45) * mm, "end": v(279.53, 214.3) * mm});
            skArc(sketch, "E810", {"start": v(279.53, 214.3) * mm, "mid": v(279.59, 214.16) * mm, "end": v(279.73, 214.1) * mm});
            skLineSegment(sketch, "E811", {"start": v(279.73, 214.1) * mm, "end": v(280.03, 214.1) * mm});
            skArc(sketch, "E812", {"start": v(280.03, 214.1) * mm, "mid": v(280.38, 214.25) * mm, "end": v(280.53, 214.6) * mm});
            skLineSegment(sketch, "E813", {"start": v(280.53, 214.6) * mm, "end": v(280.53, 216.6) * mm});
            skArc(sketch, "E814", {"start": v(281.03, 217.1) * mm, "mid": v(280.67, 216.95) * mm, "end": v(280.53, 216.6) * mm});
            skLineSegment(sketch, "E815", {"start": v(281.03, 217.1) * mm, "end": v(281.76, 217.1) * mm});
            skArc(sketch, "E816", {"start": v(282.11, 216.95) * mm, "mid": v(281.95, 217.06) * mm, "end": v(281.76, 217.1) * mm});
            skLineSegment(sketch, "E817", {"start": v(282.11, 216.95) * mm, "end": v(284.38, 214.69) * mm});
            skArc(sketch, "E818", {"start": v(284.53, 214.33) * mm, "mid": v(284.5, 214.52) * mm, "end": v(284.38, 214.69) * mm});
            skLineSegment(sketch, "E819", {"start": v(284.53, 214.33) * mm, "end": v(284.53, 212.05) * mm});
            skArc(sketch, "E820", {"start": v(284.53, 212.05) * mm, "mid": v(284.54, 212) * mm, "end": v(284.56, 211.95) * mm});
            skLineSegment(sketch, "E821", {"start": v(284.56, 211.95) * mm, "end": v(285, 211.2) * mm});
            skArc(sketch, "E822", {"start": v(285, 211) * mm, "mid": v(285.02, 211.1) * mm, "end": v(285, 211.2) * mm});
            skLineSegment(sketch, "E823", {"start": v(285, 211) * mm, "end": v(284.56, 210.25) * mm});
            skArc(sketch, "E824", {"start": v(284.56, 210.25) * mm, "mid": v(284.54, 210.2) * mm, "end": v(284.53, 210.15) * mm});
            skLineSegment(sketch, "E825", {"start": v(284.53, 210.15) * mm, "end": v(284.53, 207.87) * mm});
            skArc(sketch, "E826", {"start": v(284.38, 207.51) * mm, "mid": v(284.5, 207.68) * mm, "end": v(284.53, 207.87) * mm});
            skLineSegment(sketch, "E827", {"start": v(284.38, 207.51) * mm, "end": v(282.11, 205.25) * mm});
            skArc(sketch, "E828", {"start": v(281.76, 205.1) * mm, "mid": v(281.95, 205.14) * mm, "end": v(282.11, 205.25) * mm});
            skLineSegment(sketch, "E829", {"start": v(281.76, 205.1) * mm, "end": v(281.03, 205.1) * mm});
            skArc(sketch, "E830", {"start": v(280.53, 205.6) * mm, "mid": v(280.67, 205.25) * mm, "end": v(281.03, 205.1) * mm});
            skLineSegment(sketch, "E831", {"start": v(280.53, 205.6) * mm, "end": v(280.53, 207.6) * mm});
            skArc(sketch, "E832", {"start": v(280.53, 207.6) * mm, "mid": v(280.38, 207.95) * mm, "end": v(280.03, 208.1) * mm});
            skLineSegment(sketch, "E833", {"start": v(280.03, 208.1) * mm, "end": v(279.73, 208.1) * mm});
            skArc(sketch, "E834", {"start": v(279.73, 208.1) * mm, "mid": v(279.59, 208.04) * mm, "end": v(279.53, 207.9) * mm});
            skLineSegment(sketch, "E835", {"start": v(279.53, 207.9) * mm, "end": v(279.53, 207.75) * mm});
            skArc(sketch, "E836", {"start": v(279.33, 207.55) * mm, "mid": v(279.47, 207.6) * mm, "end": v(279.53, 207.75) * mm});
            skLineSegment(sketch, "E837", {"start": v(279.33, 207.55) * mm, "end": v(279.23, 207.55) * mm});
            skArc(sketch, "E838", {"start": v(279.23, 207.55) * mm, "mid": v(279.09, 207.5) * mm, "end": v(279.03, 207.35) * mm});
            skLineSegment(sketch, "E839", {"start": v(279.03, 207.35) * mm, "end": v(279.03, 202.6) * mm});
            skArc(sketch, "E840", {"start": v(279.03, 202.6) * mm, "mid": v(279.47, 201.54) * mm, "end": v(280.53, 201.1) * mm});
            skLineSegment(sketch, "E841", {"start": v(280.53, 201.1) * mm, "end": v(285.28, 201.1) * mm});
            skArc(sketch, "E842", {"start": v(285.28, 201.1) * mm, "mid": v(285.42, 201.16) * mm, "end": v(285.48, 201.3) * mm});
            skLineSegment(sketch, "E843", {"start": v(285.48, 201.3) * mm, "end": v(285.48, 201.4) * mm});
            skArc(sketch, "E844", {"start": v(285.68, 201.6) * mm, "mid": v(285.54, 201.54) * mm, "end": v(285.48, 201.4) * mm});
            skLineSegment(sketch, "E845", {"start": v(285.68, 201.6) * mm, "end": v(285.83, 201.6) * mm});
            skArc(sketch, "E846", {"start": v(285.83, 201.6) * mm, "mid": v(285.97, 201.66) * mm, "end": v(286.03, 201.8) * mm});
            skLineSegment(sketch, "E847", {"start": v(286.03, 201.8) * mm, "end": v(286.03, 202.1) * mm});
            skArc(sketch, "E848", {"start": v(286.03, 202.1) * mm, "mid": v(285.88, 202.45) * mm, "end": v(285.53, 202.6) * mm});
            skLineSegment(sketch, "E849", {"start": v(285.53, 202.6) * mm, "end": v(283.53, 202.6) * mm});
            skArc(sketch, "E850", {"start": v(283.03, 203.1) * mm, "mid": v(283.17, 202.75) * mm, "end": v(283.53, 202.6) * mm});
            skLineSegment(sketch, "E851", {"start": v(283.03, 203.1) * mm, "end": v(283.03, 203.83) * mm});
            skArc(sketch, "E852", {"start": v(283.17, 204.19) * mm, "mid": v(283.07, 204.02) * mm, "end": v(283.03, 203.83) * mm});
            skLineSegment(sketch, "E853", {"start": v(283.17, 204.19) * mm, "end": v(285.44, 206.45) * mm});
            skArc(sketch, "E854", {"start": v(285.8, 206.6) * mm, "mid": v(285.6, 206.56) * mm, "end": v(285.44, 206.45) * mm});
            skLineSegment(sketch, "E855", {"start": v(285.8, 206.6) * mm, "end": v(288.07, 206.6) * mm});
            skArc(sketch, "E856", {"start": v(288.07, 206.6) * mm, "mid": v(288.13, 206.6) * mm, "end": v(288.17, 206.63) * mm});
            skLineSegment(sketch, "E857", {"start": v(288.17, 206.63) * mm, "end": v(288.93, 207.06) * mm});
            skArc(sketch, "E858", {"start": v(289.13, 207.06) * mm, "mid": v(289.03, 207.09) * mm, "end": v(288.93, 207.06) * mm});
            skLineSegment(sketch, "E859", {"start": v(289.13, 207.06) * mm, "end": v(289.88, 206.63) * mm});
            skArc(sketch, "E860", {"start": v(289.88, 206.63) * mm, "mid": v(289.93, 206.6) * mm, "end": v(289.98, 206.6) * mm});
            skLineSegment(sketch, "E861", {"start": v(289.98, 206.6) * mm, "end": v(292.26, 206.6) * mm});
            skArc(sketch, "E862", {"start": v(292.61, 206.45) * mm, "mid": v(292.45, 206.56) * mm, "end": v(292.26, 206.6) * mm});
            skLineSegment(sketch, "E863", {"start": v(292.61, 206.45) * mm, "end": v(294.88, 204.19) * mm});
            skArc(sketch, "E864", {"start": v(295.03, 203.83) * mm, "mid": v(295, 204.02) * mm, "end": v(294.88, 204.19) * mm});
            skLineSegment(sketch, "E865", {"start": v(295.03, 203.83) * mm, "end": v(295.03, 203.1) * mm});
            skArc(sketch, "E866", {"start": v(294.53, 202.6) * mm, "mid": v(294.88, 202.75) * mm, "end": v(295.03, 203.1) * mm});
            skLineSegment(sketch, "E867", {"start": v(294.53, 202.6) * mm, "end": v(292.53, 202.6) * mm});
            skArc(sketch, "E868", {"start": v(292.53, 202.6) * mm, "mid": v(292.17, 202.45) * mm, "end": v(292.03, 202.1) * mm});
            skLineSegment(sketch, "E869", {"start": v(292.03, 202.1) * mm, "end": v(292.03, 201.8) * mm});
            skArc(sketch, "E870", {"start": v(292.03, 201.8) * mm, "mid": v(292.09, 201.66) * mm, "end": v(292.23, 201.6) * mm});
            skLineSegment(sketch, "E871", {"start": v(292.23, 201.6) * mm, "end": v(292.38, 201.6) * mm});
            skArc(sketch, "E872", {"start": v(292.58, 201.4) * mm, "mid": v(292.52, 201.54) * mm, "end": v(292.38, 201.6) * mm});
            skLineSegment(sketch, "E873", {"start": v(292.58, 201.4) * mm, "end": v(292.58, 201.3) * mm});
            skArc(sketch, "E874", {"start": v(292.58, 201.3) * mm, "mid": v(292.64, 201.16) * mm, "end": v(292.78, 201.1) * mm});
            skLineSegment(sketch, "E875", {"start": v(292.78, 201.1) * mm, "end": v(297.53, 201.1) * mm});
            skArc(sketch, "E876", {"start": v(297.53, 201.1) * mm, "mid": v(298.59, 201.54) * mm, "end": v(299.03, 202.6) * mm});
            skLineSegment(sketch, "E877", {"start": v(299.03, 202.6) * mm, "end": v(299.03, 207.35) * mm});
            skArc(sketch, "E878", {"start": v(299.03, 207.35) * mm, "mid": v(298.97, 207.5) * mm, "end": v(298.83, 207.55) * mm});
            skLineSegment(sketch, "E879", {"start": v(298.83, 207.55) * mm, "end": v(298.73, 207.55) * mm});
            skArc(sketch, "E880", {"start": v(298.53, 207.75) * mm, "mid": v(298.59, 207.6) * mm, "end": v(298.73, 207.55) * mm});
            skLineSegment(sketch, "E881", {"start": v(298.53, 207.75) * mm, "end": v(298.53, 207.9) * mm});
            skArc(sketch, "E882", {"start": v(298.53, 207.9) * mm, "mid": v(298.47, 208.04) * mm, "end": v(298.33, 208.1) * mm});
            skLineSegment(sketch, "E883", {"start": v(298.33, 208.1) * mm, "end": v(298.03, 208.1) * mm});
            skArc(sketch, "E884", {"start": v(298.03, 208.1) * mm, "mid": v(297.67, 207.95) * mm, "end": v(297.53, 207.6) * mm});
            skLineSegment(sketch, "E885", {"start": v(297.53, 207.6) * mm, "end": v(297.53, 205.6) * mm});
            skArc(sketch, "E886", {"start": v(297.03, 205.1) * mm, "mid": v(297.38, 205.25) * mm, "end": v(297.53, 205.6) * mm});
            skLineSegment(sketch, "E887", {"start": v(297.03, 205.1) * mm, "end": v(296.3, 205.1) * mm});
            skArc(sketch, "E888", {"start": v(295.94, 205.25) * mm, "mid": v(296.1, 205.14) * mm, "end": v(296.3, 205.1) * mm});
            skLineSegment(sketch, "E889", {"start": v(295.94, 205.25) * mm, "end": v(293.67, 207.51) * mm});
            skArc(sketch, "E890", {"start": v(293.53, 207.87) * mm, "mid": v(293.57, 207.68) * mm, "end": v(293.67, 207.51) * mm});
            skLineSegment(sketch, "E891", {"start": v(293.53, 207.87) * mm, "end": v(293.53, 210.15) * mm});
            skArc(sketch, "E892", {"start": v(293.53, 210.15) * mm, "mid": v(293.52, 210.2) * mm, "end": v(293.5, 210.25) * mm});
            skLineSegment(sketch, "E893", {"start": v(293.5, 210.25) * mm, "end": v(293.07, 211) * mm});
            skArc(sketch, "E894", {"start": v(293.07, 211.2) * mm, "mid": v(293.04, 211.1) * mm, "end": v(293.07, 211) * mm});
            skLineSegment(sketch, "E895", {"start": v(293.07, 211.2) * mm, "end": v(293.5, 211.95) * mm});
            skArc(sketch, "E896", {"start": v(293.5, 211.95) * mm, "mid": v(293.52, 212) * mm, "end": v(293.53, 212.05) * mm});
            skLineSegment(sketch, "E897", {"start": v(293.53, 212.05) * mm, "end": v(293.53, 214.33) * mm});
            skArc(sketch, "E898", {"start": v(293.67, 214.69) * mm, "mid": v(293.57, 214.52) * mm, "end": v(293.53, 214.33) * mm});
            skLineSegment(sketch, "E899", {"start": v(293.67, 214.69) * mm, "end": v(295.94, 216.95) * mm});
            skArc(sketch, "E900", {"start": v(296.3, 217.1) * mm, "mid": v(296.1, 217.06) * mm, "end": v(295.94, 216.95) * mm});
            skLineSegment(sketch, "E901", {"start": v(296.3, 217.1) * mm, "end": v(297.03, 217.1) * mm});
            skArc(sketch, "E902", {"start": v(297.53, 216.6) * mm, "mid": v(297.38, 216.95) * mm, "end": v(297.03, 217.1) * mm});
            skLineSegment(sketch, "E903", {"start": v(297.53, 216.6) * mm, "end": v(297.53, 214.6) * mm});
            skArc(sketch, "E904", {"start": v(297.53, 214.6) * mm, "mid": v(297.67, 214.25) * mm, "end": v(298.03, 214.1) * mm});
            skLineSegment(sketch, "E905", {"start": v(298.03, 214.1) * mm, "end": v(298.33, 214.1) * mm});
            skArc(sketch, "E906", {"start": v(298.33, 214.1) * mm, "mid": v(298.47, 214.16) * mm, "end": v(298.53, 214.3) * mm});
            skLineSegment(sketch, "E907", {"start": v(298.53, 214.3) * mm, "end": v(298.53, 214.45) * mm});
            skArc(sketch, "E908", {"start": v(298.73, 214.65) * mm, "mid": v(298.59, 214.6) * mm, "end": v(298.53, 214.45) * mm});
            skLineSegment(sketch, "E909", {"start": v(298.73, 214.65) * mm, "end": v(298.83, 214.65) * mm});
            skArc(sketch, "E910", {"start": v(298.83, 214.65) * mm, "mid": v(298.97, 214.7) * mm, "end": v(299.03, 214.85) * mm});
            skLineSegment(sketch, "E911", {"start": v(299.03, 214.85) * mm, "end": v(299.03, 219.6) * mm});
            skArc(sketch, "E912", {"start": v(299.03, 219.6) * mm, "mid": v(298.59, 220.66) * mm, "end": v(297.53, 221.1) * mm});
            skLineSegment(sketch, "E913", {"start": v(297.53, 221.1) * mm, "end": v(292.78, 221.1) * mm});
            skArc(sketch, "E914", {"start": v(292.78, 221.1) * mm, "mid": v(292.64, 221.04) * mm, "end": v(292.58, 220.9) * mm});
            skLineSegment(sketch, "E915", {"start": v(292.58, 220.9) * mm, "end": v(292.58, 220.8) * mm});
            skArc(sketch, "E916", {"start": v(292.38, 220.6) * mm, "mid": v(292.52, 220.66) * mm, "end": v(292.58, 220.8) * mm});
            skLineSegment(sketch, "E917", {"start": v(292.38, 220.6) * mm, "end": v(292.23, 220.6) * mm});
            skArc(sketch, "E918", {"start": v(292.23, 220.6) * mm, "mid": v(292.09, 220.54) * mm, "end": v(292.03, 220.4) * mm});
            skLineSegment(sketch, "E919", {"start": v(292.03, 220.4) * mm, "end": v(292.03, 220.1) * mm});
            skArc(sketch, "E920", {"start": v(292.03, 220.1) * mm, "mid": v(292.17, 219.75) * mm, "end": v(292.53, 219.6) * mm});
            skLineSegment(sketch, "E921", {"start": v(292.53, 219.6) * mm, "end": v(294.53, 219.6) * mm});
            skArc(sketch, "E922", {"start": v(295.03, 219.1) * mm, "mid": v(294.88, 219.45) * mm, "end": v(294.53, 219.6) * mm});
            skLineSegment(sketch, "E923", {"start": v(295.03, 219.1) * mm, "end": v(295.03, 218.37) * mm});
            skArc(sketch, "E924", {"start": v(294.88, 218.01) * mm, "mid": v(295, 218.18) * mm, "end": v(295.03, 218.37) * mm});
            skLineSegment(sketch, "E925", {"start": v(294.88, 218.01) * mm, "end": v(292.61, 215.75) * mm});
            skArc(sketch, "E926", {"start": v(292.26, 215.6) * mm, "mid": v(292.45, 215.64) * mm, "end": v(292.61, 215.75) * mm});
            skLineSegment(sketch, "E927", {"start": v(292.26, 215.6) * mm, "end": v(289.98, 215.6) * mm});
            skArc(sketch, "E928", {"start": v(289.98, 215.6) * mm, "mid": v(289.93, 215.6) * mm, "end": v(289.88, 215.57) * mm});
            skLineSegment(sketch, "E929", {"start": v(289.88, 215.57) * mm, "end": v(289.13, 215.14) * mm});
            skArc(sketch, "E930", {"start": v(288.93, 215.14) * mm, "mid": v(289.03, 215.11) * mm, "end": v(289.13, 215.14) * mm});
            skLineSegment(sketch, "E931", {"start": v(288.93, 215.14) * mm, "end": v(288.17, 215.57) * mm});
            skArc(sketch, "E932", {"start": v(288.17, 215.57) * mm, "mid": v(288.13, 215.6) * mm, "end": v(288.07, 215.6) * mm});
            skLineSegment(sketch, "E933", {"start": v(288.07, 215.6) * mm, "end": v(285.8, 215.6) * mm});
            skArc(sketch, "E934", {"start": v(285.44, 215.75) * mm, "mid": v(285.6, 215.64) * mm, "end": v(285.8, 215.6) * mm});
            skLineSegment(sketch, "E935", {"start": v(285.44, 215.75) * mm, "end": v(283.17, 218.01) * mm});
            skArc(sketch, "E936", {"start": v(283.03, 218.37) * mm, "mid": v(283.07, 218.18) * mm, "end": v(283.17, 218.01) * mm});
            skLineSegment(sketch, "E937", {"start": v(283.03, 218.37) * mm, "end": v(283.03, 219.1) * mm});
            skArc(sketch, "E938", {"start": v(283.53, 219.6) * mm, "mid": v(283.17, 219.45) * mm, "end": v(283.03, 219.1) * mm});
            skLineSegment(sketch, "E939", {"start": v(283.53, 219.6) * mm, "end": v(285.53, 219.6) * mm});
            skArc(sketch, "E940", {"start": v(285.53, 219.6) * mm, "mid": v(285.88, 219.75) * mm, "end": v(286.03, 220.1) * mm});
            skLineSegment(sketch, "E941", {"start": v(286.03, 220.1) * mm, "end": v(286.03, 220.4) * mm});
            skArc(sketch, "E942", {"start": v(286.03, 220.4) * mm, "mid": v(285.97, 220.54) * mm, "end": v(285.83, 220.6) * mm});
            skLineSegment(sketch, "E943", {"start": v(285.83, 220.6) * mm, "end": v(285.68, 220.6) * mm});
            skArc(sketch, "E944", {"start": v(285.48, 220.8) * mm, "mid": v(285.54, 220.66) * mm, "end": v(285.68, 220.6) * mm});
            skLineSegment(sketch, "E945", {"start": v(285.48, 220.8) * mm, "end": v(285.48, 220.9) * mm});
            skArc(sketch, "E946", {"start": v(285.48, 220.9) * mm, "mid": v(285.42, 221.04) * mm, "end": v(285.28, 221.1) * mm});
            skLineSegment(sketch, "E947", {"start": v(285.28, 221.1) * mm, "end": v(280.53, 221.1) * mm});
            skArc(sketch, "E948", {"start": v(287.11, 214.09) * mm, "mid": v(286.52, 213.6) * mm, "end": v(286.04, 213) * mm});
            skLineSegment(sketch, "E949", {"start": v(287.77, 213.55) * mm, "end": v(287.11, 214.09) * mm});
            skArc(sketch, "E950", {"start": v(290.29, 213.55) * mm, "mid": v(289.03, 213.85) * mm, "end": v(287.77, 213.55) * mm});
            skLineSegment(sketch, "E951", {"start": v(290.94, 214.09) * mm, "end": v(290.29, 213.55) * mm});
            skArc(sketch, "E952", {"start": v(292.02, 213) * mm, "mid": v(291.54, 213.6) * mm, "end": v(290.94, 214.09) * mm});
            skLineSegment(sketch, "E953", {"start": v(291.47, 212.36) * mm, "end": v(292.02, 213) * mm});
            skArc(sketch, "E954", {"start": v(291.47, 209.84) * mm, "mid": v(291.78, 211.1) * mm, "end": v(291.47, 212.36) * mm});
            skLineSegment(sketch, "E955", {"start": v(292.02, 209.2) * mm, "end": v(291.47, 209.84) * mm});
            skArc(sketch, "E956", {"start": v(290.94, 208.11) * mm, "mid": v(291.54, 208.6) * mm, "end": v(292.02, 209.2) * mm});
            skLineSegment(sketch, "E957", {"start": v(290.29, 208.65) * mm, "end": v(290.94, 208.11) * mm});
            skArc(sketch, "E958", {"start": v(287.77, 208.65) * mm, "mid": v(289.03, 208.35) * mm, "end": v(290.29, 208.65) * mm});
            skLineSegment(sketch, "E959", {"start": v(287.11, 208.11) * mm, "end": v(287.77, 208.65) * mm});
            skArc(sketch, "E960", {"start": v(286.04, 209.2) * mm, "mid": v(286.52, 208.6) * mm, "end": v(287.11, 208.11) * mm});
            skLineSegment(sketch, "E961", {"start": v(286.58, 209.84) * mm, "end": v(286.04, 209.2) * mm});
            skArc(sketch, "E962", {"start": v(286.58, 212.36) * mm, "mid": v(286.28, 211.1) * mm, "end": v(286.58, 209.84) * mm});
            skLineSegment(sketch, "E963", {"start": v(286.04, 213) * mm, "end": v(286.58, 212.36) * mm});
            skSolve(sketch);
        }
        {
            var Q0;
            Q0=makeQuery(id+"F11.imprint","IMPRINT",FACE,{"disambiguationData":[TD([[makeQuery(id+"F11.imprint","IMPRINT",EDGE,{"derivedFrom":sQuery(id+"F11.wireOp",EDGE,"E804")}),1.0]])]});
            var Q1;
            Q1=makeQuery(id+"F11.imprint","IMPRINT",FACE,{"disambiguationData":[TD([[makeQuery(id+"F11.imprint","IMPRINT",EDGE,{"derivedFrom":sQuery(id+"F11.wireOp",EDGE,"E324")}),1.0]])]});
            var Q2;
            Q2=makeQuery(id+"F11.imprint","IMPRINT",FACE,{"disambiguationData":[TD([[makeQuery(id+"F11.imprint","IMPRINT",EDGE,{"derivedFrom":sQuery(id+"F11.wireOp",EDGE,"E484")}),1.0]])]});
            var Q3;
            Q3=makeQuery(id+"F11.imprint","IMPRINT",FACE,{"disambiguationData":[TD([[makeQuery(id+"F11.imprint","IMPRINT",EDGE,{"derivedFrom":sQuery(id+"F11.wireOp",EDGE,"E644")}),1.0]])]});
            extrude(context, id + "F12", {"entities" : qUnion([Q0, Q1, Q2, Q3]), "oppositeDirection" : true, "depth" : 42 * mm, "offsetDistance" : 25 * mm, "hasSecondDirection" : true, "secondDirectionOppositeDirection" : false, "secondDirectionDepth" : 20 * mm});
        }
    });
